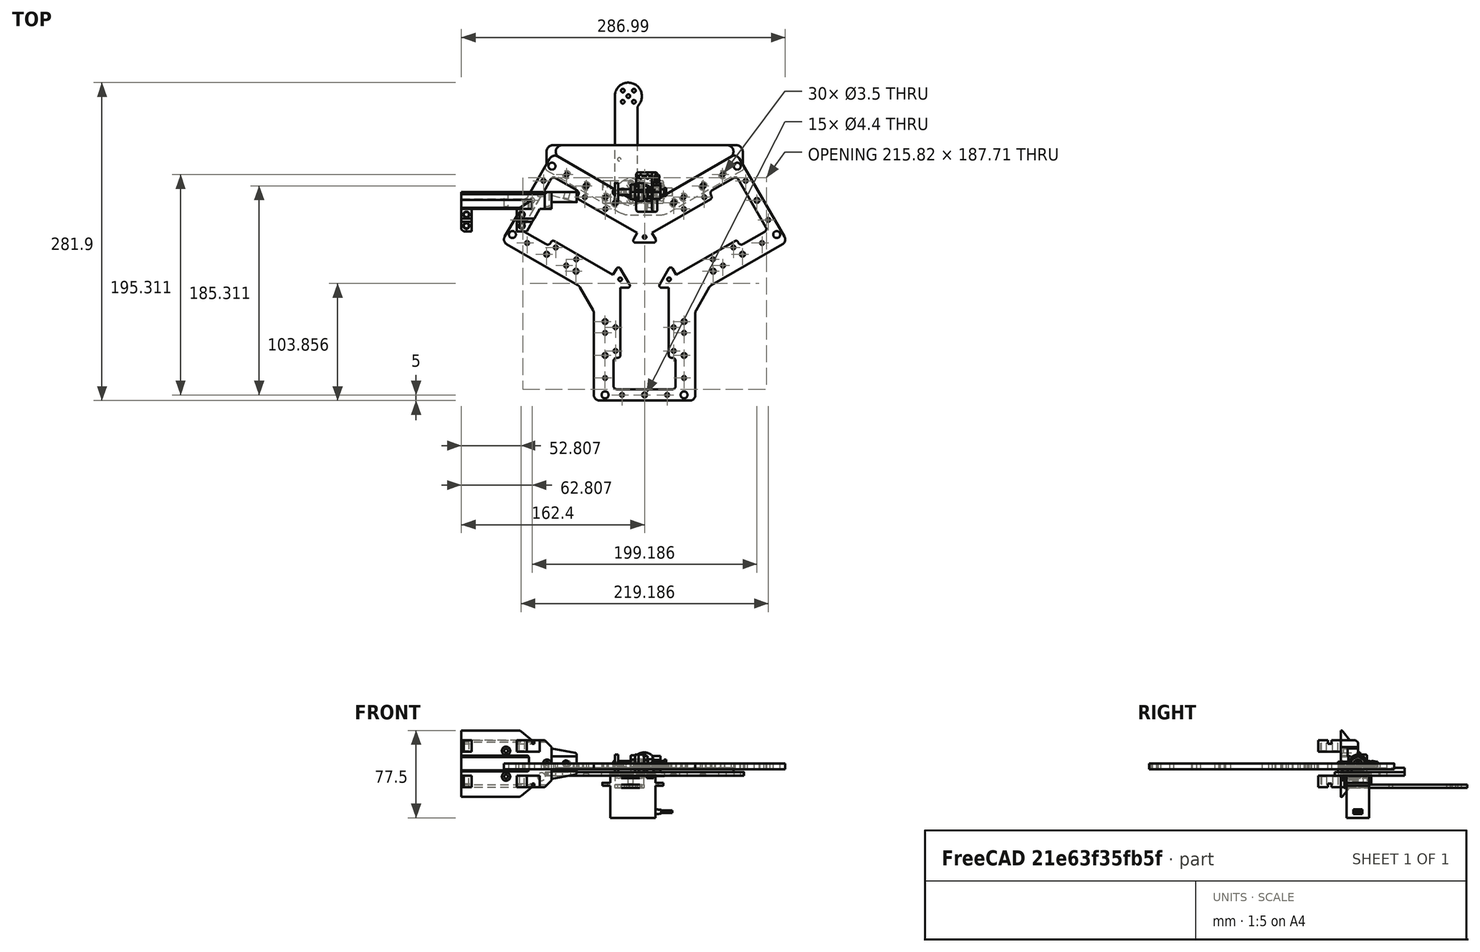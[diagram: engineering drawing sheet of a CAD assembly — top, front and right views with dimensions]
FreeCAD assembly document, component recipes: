
FREECAD ASSEMBLY — COMPONENT RECIPES ("twin-actuator")

This assembly document has 21 components, labeled P0..P20 below (a component is one placed body or linked part). 19 of them carry a construction recipe — the FreeCAD feature program that regenerates the part from scratch, quoted from this document or its linked companion documents; the rest are supplied as boundary geometry only. No exploded tour is included for this assembly.
COMPONENT P0 — recipe-attached ("Axe001", modeled in this document).
Construction recipe (the document's own serialized feature program — sketch geometry with constraints, then the solid features built on it; lengths are millimeters unless a unit is written):

FEATURE [Sketcher::SketchObject] Sketch
  ArcFitTolerance = 0
  AttachmentSupport = -> [XZ_Plane]
  ExternalTypes = [0]
  FullyConstrained = true
  MakeInternals = false
  MapMode = 5
  Placement = pos=(0,0,0) rot=(1,0,0;1.5708rad)
  sketch-geometry (14):
    g0: LineSegment StartX=0 StartY=2.5 StartZ=0 EndX=3 EndY=2.5 EndZ=0
    g1: LineSegment StartX=3 StartY=2.5 StartZ=0 EndX=3 EndY=3.5 EndZ=0
    g2: LineSegment StartX=3 StartY=3.5 StartZ=0 EndX=5 EndY=3.5 EndZ=0
    g3: LineSegment StartX=5 StartY=3.5 StartZ=0 EndX=5 EndY=1.5 EndZ=0
    g4: LineSegment StartX=5 StartY=1.5 StartZ=0 EndX=-9 EndY=1.5 EndZ=0
    g5: LineSegment StartX=-9 StartY=1.5 StartZ=0 EndX=-9 EndY=0 EndZ=0
    g6: LineSegment StartX=-9 StartY=0 StartZ=0 EndX=-37.5 EndY=0 EndZ=0
    g7: LineSegment StartX=-37.5 StartY=0 StartZ=0 EndX=-37.5 EndY=2.5 EndZ=0
    g8: LineSegment StartX=-37.5 StartY=2.5 StartZ=0 EndX=-11 EndY=2.5 EndZ=0
    g9: LineSegment StartX=-11 StartY=2.5 StartZ=0 EndX=-11 EndY=4 EndZ=0
    g10: LineSegment StartX=-11 StartY=4 StartZ=0 EndX=-7 EndY=4 EndZ=0
    g11: LineSegment StartX=-7 StartY=4 StartZ=0 EndX=-7 EndY=7.5 EndZ=0
    g12: LineSegment StartX=-7 StartY=7.5 StartZ=0 EndX=0 EndY=7.5 EndZ=0
    g13: LineSegment StartX=0 StartY=7.5 StartZ=0 EndX=0 EndY=2.5 EndZ=0
  constraints (42):
    c: PointOnObject(g0,g-2)
    c: Horizontal(g0)
    c: Coincident(g0,g1)
    c: Coincident(g1,g2)
    c: Horizontal(g2)
    c: Coincident(g2,g3)
    c: Vertical(g3)
    c: Coincident(g3,g4)
    c: Horizontal(g4)
    c: Coincident(g4,g5)
    c: Vertical(g5)
    c: Coincident(g5,g6)
    c: PointOnObject(g6,g-1)
    c: Horizontal(g6)
    c: Coincident(g6,g7)
    c: Vertical(g7)
    c: Coincident(g7,g8)
    c: Horizontal(g8)
    c: Coincident(g8,g9)
    c: Coincident(g9,g10)
    c: Horizontal(g10)
    c: Coincident(g10,g11)
    c: Vertical(g11)
    c: Coincident(g11,g12)
    c: Horizontal(g12)
    c: Coincident(g12,g13)
    c: Coincident(g13,g0)
    c: Vertical(g13)
    c: Vertical(g9)
    c: Vertical(g1)
    c: DistanceY(g2) = 3.5
    c: DistanceX(g2,g2) = 2
    c: DistanceX(g-1,g0) = 3
    c: DistanceY(g0) = 2.5
    c: DistanceX(g4,g4) = 14
    c: DistanceY(g3) = 1.5
    c: DistanceY(g10) = 4
    c: DistanceY(g12) = 7.5
    c: DistanceX(g12,g12) = 7
    c: DistanceX(g10,g10) = 4
    c: DistanceY(g8) = 2.5
    c: DistanceX(g6,g3) = 42.5
FEATURE [PartDesign::Revolution] Revolution
  Angle = 360
  Angle2 = 0
  Axis = (1,0,0)
  Base = (0,0,0)
  FuseOrder = 0
  Placement = pos=(0,0,0) rot=(1,0,0;1.5708rad)
  Profile = -> Sketch
  ReferenceAxis = -> X_Axis
  Refine = true
  Suppressed = false
  Type = 0
FEATURE [Sketcher::SketchObject] Sketch001
  ArcFitTolerance = 0
  AttachmentSupport = -> [YZ_Plane]
  ExternalGeometry = -> [Revolution]
  ExternalTypes = [0]
  FullyConstrained = true
  MakeInternals = false
  MapMode = 5
  Placement = pos=(0,0,0) rot=(0.57735,0.57735,0.57735;2.0944rad)
  sketch-geometry (7):
    g0: LineSegment StartX=6 StartY=3.4641 StartZ=0 EndX=0 EndY=6.9282 EndZ=0
    g1: LineSegment StartX=0 StartY=6.9282 StartZ=0 EndX=-6 EndY=3.4641 EndZ=0
    g2: LineSegment StartX=-6 StartY=3.4641 StartZ=0 EndX=-6 EndY=-3.4641 EndZ=0
    g3: LineSegment StartX=-6 StartY=-3.4641 StartZ=0 EndX=1.8723e-12 EndY=-6.9282 EndZ=0
    g4: LineSegment StartX=1.8723e-12 StartY=-6.9282 StartZ=0 EndX=6 EndY=-3.4641 EndZ=0
    g5: LineSegment StartX=6 StartY=-3.4641 StartZ=0 EndX=6 EndY=3.4641 EndZ=0
    g6: Circle [constr] CenterX=0 CenterY=0 CenterZ=0 NormalX=0 NormalY=0 NormalZ=1 AngleXU=0 Radius=6.9282
  constraints (16):
    c: Coincident(g0,g1)
    c: Coincident(g1,g2)
    c: Coincident(g2,g3)
    c: Coincident(g3,g4)
    c: Coincident(g4,g5)
    c: Coincident(g5,g0)
    c: Equal(g0, g1-g5) x5
    c: PointOnObject(g0,g6)
    c: PointOnObject(g1,g6)
    c: PointOnObject(g2,g6)
    c: PointOnObject(g3,g6)
    c: PointOnObject(g4,g6)
    c: PointOnObject(g5,g6)
    c: Coincident(g6,g-1)
    c: PointOnObject(g0,g-2)
    c: DistanceX(g1,g0) = 12
FEATURE [PartDesign::Pocket] Pocket
  BaseFeature = -> Revolution
  Direction = (-1,0,0)
  Length = 5
  Length2 = 100
  Placement = pos=(0,0,0) rot=(1,0,0;1.5708rad)
  Profile = -> Sketch001
  Refine = true
  SideType = 0
  Suppressed = false
  Type = 1
  Type2 = 0
FEATURE [Sketcher::SketchObject] Sketch002
  ArcFitTolerance = 0
  AttachmentSupport = -> [XZ_Plane]
  ExternalGeometry = -> [Pocket]
  ExternalTypes = [0]
  FullyConstrained = true
  MakeInternals = false
  MapMode = 5
  Placement = pos=(0,0,0) rot=(1,0,0;1.5708rad)
  sketch-geometry (2):
    g0: Circle CenterX=-3.5 CenterY=0 CenterZ=0 NormalX=0 NormalY=0 NormalZ=1 AngleXU=0 Radius=2.5
    g1: LineSegment [constr] StartX=-6e-16 StartY=-3.4641 StartZ=0 EndX=-7 EndY=3.4641 EndZ=0
  constraints (5):
    c: PointOnObject(g0,g-1)
    c: Diameter(g0) = 5
    c: Coincident(g1,g-4)
    c: Coincident(g1,g-3)
    c: PointOnObject(g0,g1)
FEATURE [PartDesign::Pocket] Pocket001
  BaseFeature = -> Pocket
  Direction = (0,1,-2e-16)
  Length = 5
  Length2 = 100
  Placement = pos=(0,0,0) rot=(1,0,0;1.5708rad)
  Profile = -> Sketch002
  Refine = true
  SideType = 2
  Suppressed = false
  Type = 1
  Type2 = 0
FEATURE [PartDesign::Chamfer] Chamfer
  Angle = 45
  Base = -> Pocket001 [Edge14,Edge21]
  BaseFeature = -> Pocket001
  ChamferType = 0
  FlipDirection = false
  Placement = pos=(0,0,0) rot=(1,0,0;1.5708rad)
  Refine = true
  Size = 0.2
  Size2 = 1
  SupportTransform = false
  Suppressed = false
  UseAllEdges = false
FEATURE [Sketcher::SketchObject] Sketch003
  ArcFitTolerance = 0
  AttachmentSupport = -> [Chamfer]
  ExternalTypes = [0]
  FullyConstrained = true
  MakeInternals = false
  MapMode = 5
  Placement = pos=(-37.5,0,0) rot=(0.707107,0,-0.707107;3.14159rad)
  sketch-geometry (1):
    g0: Circle CenterX=0 CenterY=0 CenterZ=0 NormalX=0 NormalY=0 NormalZ=1 AngleXU=0 Radius=1.5
  constraints (2):
    c: Coincident(g0,g-1)
    c: Diameter(g0) = 3
FEATURE [PartDesign::Pocket] Pocket002
  BaseFeature = -> Chamfer
  Direction = (1,0,2e-16)
  Length = 5
  Length2 = 100
  Placement = pos=(0,0,0) rot=(1,0,0;1.5708rad)
  Profile = -> Sketch003
  Refine = true
  SideType = 0
  Suppressed = false
  Type = 0
  Type2 = 0
FEATURE [PartDesign::Body] Body  label="Axe"
  AllowCompound = true
  Group = -> [Sketch,Revolution,Sketch001,Pocket,Sketch002,Pocket001,Chamfer,Sketch003,Pocket002]
  Origin = -> Origin105
  Placement = pos=(14.5,-1.72853e-06,0) rot=(0,0,1;0rad)
  Tip = -> Pocket002
COMPONENT P1 — same part as P0; its construction recipe is shown at P0.
COMPONENT P2 — recipe-attached ("Butée", modeled in this document).
Construction recipe (the document's own serialized feature program — sketch geometry with constraints, then the solid features built on it; lengths are millimeters unless a unit is written):

FEATURE [PartDesign::ShapeBinder] ShapeBinder001
  Placement = pos=(0.4,-64.9,0) rot=(0,0,1;3.14159rad)
  Support = -> [Part__Feature148]
  TraceSupport = false
FEATURE [Sketcher::SketchObject] Sketch265
  ArcFitTolerance = 1e-06
  AttachmentSupport = -> [ShapeBinder001]
  ExternalGeometry = -> [ShapeBinder001]
  ExternalTypes = [0,0,0,0,0,0,0,0,0]
  FullyConstrained = true
  MakeInternals = false
  MapMode = 5
  Placement = pos=(0.4,-64.9,-5) rot=(0,1,0;3.14159rad)
  sketch-geometry (12):
    g0: LineSegment [constr] StartX=0 StartY=34.0637 StartZ=0 EndX=-89.173 EndY=85.5477 EndZ=0
    g1: LineSegment [constr] StartX=0 StartY=34.0637 StartZ=0 EndX=0 EndY=106.471 EndZ=0
    g2: LineSegment StartX=0 StartY=106.471 StartZ=0 EndX=-87 EndY=106.471 EndZ=0
    g3: LineSegment StartX=-89.173 StartY=85.5477 StartZ=0 EndX=-87 EndY=89.3116 EndZ=0
    g4: LineSegment StartX=-87 StartY=89.3116 StartZ=0 EndX=-87 EndY=106.471 EndZ=0
    g5: LineSegment StartX=-89.173 StartY=85.5477 StartZ=0 EndX=-18.0263 EndY=44.4711 EndZ=0
    g6: LineSegment StartX=-18.0263 StartY=44.4711 StartZ=0 EndX=0 EndY=44.4711 EndZ=0
    g7: LineSegment StartX=0 StartY=44.4711 StartZ=0 EndX=0 EndY=106.471 EndZ=0
    g8: Circle CenterX=-69.1025 CenterY=80.3109 CenterZ=0 NormalX=0 NormalY=0 NormalZ=1 AngleXU=0 Radius=3.5
    g9: Circle CenterX=-34.4615 CenterY=60.3109 CenterZ=0 NormalX=0 NormalY=0 NormalZ=1 AngleXU=0 Radius=3.5
    g10: Circle CenterX=-51.782 CenterY=70.3109 CenterZ=0 NormalX=0 NormalY=0 NormalZ=1 AngleXU=0 Radius=1.7
    g11: Circle CenterX=-25.8013 CenterY=55.3109 CenterZ=0 NormalX=0 NormalY=0 NormalZ=1 AngleXU=0 Radius=1.7
  constraints (31):
    c: PointOnObject(g0,g-2)
    c: Coincident(g1,g0)
    c: PointOnObject(g1,g-2)
    c: Parallel(g0,g-8)
    c: Distance(g0,g-9) = 2
    c: Distance(g1,g-10) = 47
    c: Coincident(g2,g1)
    c: Horizontal(g2)
    c: PointOnObject(g0,g-11)
    c: Coincident(g3,g0)
    c: PointOnObject(g3,g-11)
    c: Coincident(g4,g3)
    c: Coincident(g4,g2)
    c: Vertical(g4)
    c: DistanceX(g2,g2) = 87
    c: Coincident(g5,g0)
    c: PointOnObject(g5,g0)
    c: Coincident(g6,g5)
    c: PointOnObject(g6,g1)
    c: Coincident(g7,g6)
    c: Coincident(g7,g1)
    c: Horizontal(g6)
    c: Distance(g-10,g6) = 15
    c: Coincident(g8,g-3)
    c: Coincident(g9,g-5)
    c: Equal(g8,g9)
    c: Diameter(g8) = 7
    c: Coincident(g10,g-4)
    c: Coincident(g11,g-6)
    c: Equal(g11,g10)
    c: Diameter(g10) = 3.4
FEATURE [PartDesign::Pad] Pad113
  Direction = (0,0,-1)
  Length = 3
  Length2 = 10
  Placement = pos=(0.4,-64.9,0) rot=(0,0,1;3.14159rad)
  Profile = -> Sketch265
  ReferenceAxis = -> Sketch265 [N_Axis]
  Refine = true
  SideType = 0
  Suppressed = false
  Type = 0
  Type2 = 0
FEATURE [PartDesign::Fillet] Fillet031
  Base = -> Pad113 [Edge11]
  BaseFeature = -> Pad113
  Placement = pos=(0.4,-64.9,0) rot=(0,0,1;3.14159rad)
  Radius = 6
  Refine = true
  SupportTransform = false
  Suppressed = false
  UseAllEdges = false
FEATURE [PartDesign::Fillet] Fillet032
  Base = -> Fillet031 [Edge31,Edge29]
  BaseFeature = -> Fillet031
  Placement = pos=(0.4,-64.9,0) rot=(0,0,1;3.14159rad)
  Radius = 3
  Refine = true
  SupportTransform = false
  Suppressed = false
  UseAllEdges = false
FEATURE [PartDesign::Fillet] Fillet033
  Base = -> Fillet032 [Edge30]
  BaseFeature = -> Fillet032
  Placement = pos=(0.4,-64.9,0) rot=(0,0,1;3.14159rad)
  Radius = 20
  Refine = true
  SupportTransform = false
  Suppressed = false
  UseAllEdges = false
FEATURE [Sketcher::SketchObject] Sketch266
  ArcFitTolerance = 1e-06
  AttachmentSupport = -> [Fillet033]
  ExternalGeometry = -> [ShapeBinder001,Fillet033]
  ExternalTypes = [0,0,0,0,0]
  FullyConstrained = true
  MakeInternals = false
  MapMode = 5
  Placement = pos=(0.4,-64.9,-5) rot=(0,0,1;3.14159rad)
  sketch-geometry (5):
    g0: LineSegment StartX=1.3e-14 StartY=-106.471 StartZ=0 EndX=7.3e-15 EndY=-59.4711 EndZ=0
    g1: LineSegment StartX=7.3e-15 StartY=-59.4711 StartZ=0 EndX=-11.6673 EndY=-59.4711 EndZ=0
    g2: LineSegment StartX=-14.1673 StartY=-60.141 StartZ=0 EndX=-75.8689 EndY=-95.7644 EndZ=0
    g3: LineSegment StartX=1.3e-14 StartY=-106.471 StartZ=0 EndX=-73 EndY=-106.471 EndZ=0
    g4: ArcOfCircle CenterX=-73 CenterY=-100.733 CenterZ=0 NormalX=0 NormalY=0 NormalZ=1 AngleXU=0 Radius=5.73771 StartAngle=2.0944 EndAngle=4.71239
  constraints (11):
    c: Coincident(g-7,g0)
    c: PointOnObject(g0,g-6)
    c: Coincident(g0,g1)
    c: Coincident(g1,g-5)
    c: Horizontal(g1)
    c: Tangent(g-4,g2) = -1.5708
    c: Coincident(g3,g0)
    c: PointOnObject(g3,g-7)
    c: Tangent(g4,g2) = -1.5708
    c: Tangent(g4,g3) = 1.5708
    c: DistanceX(g-7,g3) = 8
FEATURE [PartDesign::Pad] Pad114
  BaseFeature = -> Fillet033
  Direction = (0,0,1)
  Length = 4
  Length2 = 10
  Placement = pos=(0.4,-64.9,0) rot=(0,0,1;3.14159rad)
  Profile = -> Sketch266
  ReferenceAxis = -> Sketch266 [N_Axis]
  Refine = true
  SideType = 0
  Suppressed = false
  Type = 0
  Type2 = 0
FEATURE [PartDesign::Mirrored] Mirrored001
  BaseFeature = -> Pad114
  MirrorPlane = -> Sketch265 [V_Axis]
  Originals = -> [Pad113,Fillet031,Fillet032,Fillet033,Pad114]
  Placement = pos=(0.4,-64.9,0) rot=(0,0,1;3.14159rad)
  Refine = true
  Suppressed = false
  TransformMode = 1
FEATURE [PartDesign::Chamfer] Chamfer040
  Angle = 45
  Base = -> Mirrored001 [Edge92,Edge94,Edge96,Edge98]
  BaseFeature = -> Mirrored001
  ChamferType = 0
  FlipDirection = false
  Placement = pos=(0.4,-64.9,0) rot=(0,0,1;3.14159rad)
  Refine = true
  Size = 2
  Size2 = 1
  SupportTransform = false
  Suppressed = false
  UseAllEdges = false
FEATURE [PartDesign::Body] Body046  label="Butée"
  AllowCompound = true
  Group = -> [ShapeBinder001,Sketch265,Pad113,Fillet031,Fillet032,Fillet033,Sketch266,Pad114,Mirrored001,Chamfer040]
  Origin = -> Origin159
  Placement = pos=(0,0,-2.63) rot=(0,0,1;0rad)
  Tip = -> Chamfer040
COMPONENT P3 — recipe-attached ("Color_Sensor_Support001", modeled in this document).
Construction recipe (the document's own serialized feature program — sketch geometry with constraints, then the solid features built on it; lengths are millimeters unless a unit is written):

FEATURE [PartDesign::SubShapeBinder] Binder001
  BindCopyOnChange = 0
  BindMode = 0
  ClaimChildren = false
  Context = -> Part [Body045.Binder001.]
  Fuse = false
  MakeFace = true
  OffsetFill = false
  OffsetIntersection = false
  OffsetJoinType = 0
  OffsetOpenResult = false
  PartialLoad = false
  Refine = true
  Relative = true
  Support = -> [Link[Body.Fillet001.Face1]]
  _Version = 2
FEATURE [Sketcher::SketchObject] Sketch259
  ArcFitTolerance = 1e-06
  AttachmentSupport = -> [Origin157]
  ExternalGeometry = -> [Binder001]
  ExternalTypes = [0,0,0,0]
  FullyConstrained = true
  MakeInternals = false
  MapMode = 5
  sketch-geometry (6):
    g0: LineSegment StartX=-7 StartY=17.5 StartZ=0 EndX=-7 EndY=-17.5 EndZ=0
    g1: LineSegment StartX=-7 StartY=-17.5 StartZ=0 EndX=11.5 EndY=-17.5 EndZ=0
    g2: LineSegment StartX=11.5 StartY=-17.5 StartZ=0 EndX=11.5 EndY=17.5 EndZ=0
    g3: LineSegment StartX=11.5 StartY=17.5 StartZ=0 EndX=-7 EndY=17.5 EndZ=0
    g4: Circle CenterX=-3 CenterY=13.5 CenterZ=0 NormalX=0 NormalY=0 NormalZ=1 AngleXU=0 Radius=1.7
    g5: Circle CenterX=3 CenterY=13.5 CenterZ=0 NormalX=0 NormalY=0 NormalZ=1 AngleXU=0 Radius=1.7
  constraints (16):
    c: Coincident(g0,g1)
    c: Coincident(g1,g2)
    c: Coincident(g2,g3)
    c: Coincident(g3,g0)
    c: Vertical(g0)
    c: Vertical(g2)
    c: Horizontal(g1)
    c: Horizontal(g3)
    c: PointOnObject(g-3,g0)
    c: PointOnObject(g-4,g3)
    c: Distance(g2,g-5) = 4.5
    c: DistanceY(g0,g0) = 35
    c: Coincident(g4,g-6)
    c: Diameter(g4) = 3.4
    c: Equal(g5,g4)
    c: Symmetric(g5,g4,g-2)
FEATURE [PartDesign::Pad] Pad110
  Direction = (0,0,1)
  Length = 3
  Length2 = 10
  Profile = -> Sketch259
  ReferenceAxis = -> Sketch259 [N_Axis]
  Refine = true
  Reversed = true
  SideType = 0
  Suppressed = false
  Type = 0
  Type2 = 0
FEATURE [Sketcher::SketchObject] Sketch260
  ArcFitTolerance = 1e-06
  AttachmentSupport = -> [Pad110]
  ExternalGeometry = -> [Pad110]
  ExternalTypes = [0]
  FullyConstrained = true
  MakeInternals = false
  MapMode = 5
  sketch-geometry (4):
    g0: LineSegment StartX=11.5 StartY=17.5 StartZ=0 EndX=7 EndY=17.5 EndZ=0
    g1: LineSegment StartX=7 StartY=17.5 StartZ=0 EndX=7 EndY=-17.5 EndZ=0
    g2: LineSegment StartX=7 StartY=-17.5 StartZ=0 EndX=11.5 EndY=-17.5 EndZ=0
    g3: LineSegment StartX=11.5 StartY=-17.5 StartZ=0 EndX=11.5 EndY=17.5 EndZ=0
  constraints (10):
    c: Coincident(g0,g1)
    c: Coincident(g1,g2)
    c: Coincident(g2,g3)
    c: Coincident(g3,g0)
    c: Horizontal(g0)
    c: Horizontal(g2)
    c: Vertical(g1)
    c: Coincident(g0,g-3)
    c: Coincident(g2,g-3)
    c: Distance(g0,g0) = 4.5
FEATURE [PartDesign::Pad] Pad111
  BaseFeature = -> Pad110
  Direction = (0,0,1)
  Length = 1.6
  Length2 = 10
  Profile = -> Sketch260
  ReferenceAxis = -> Sketch260 [N_Axis]
  Refine = true
  SideType = 0
  Suppressed = false
  Type = 0
  Type2 = 0
FEATURE [PartDesign::Fillet] Fillet029
  Base = -> Pad111 [Edge2,Edge1,Edge15,Edge16]
  BaseFeature = -> Pad111
  Radius = 2
  Refine = true
  SupportTransform = false
  Suppressed = false
  UseAllEdges = false
FEATURE [Sketcher::SketchObject] Sketch261
  ArcFitTolerance = 1e-06
  AttachmentSupport = -> [Fillet029]
  ExternalTypes = [0]
  FullyConstrained = true
  MakeInternals = false
  MapMode = 5
  sketch-geometry (8):
    g0: ArcOfCircle CenterX=-5.52 CenterY=13.51 CenterZ=0 NormalX=0 NormalY=0 NormalZ=1 AngleXU=0 Radius=1 StartAngle=1.5708 EndAngle=4.71239
    g1: ArcOfCircle CenterX=5.52 CenterY=13.51 CenterZ=0 NormalX=0 NormalY=0 NormalZ=1 AngleXU=0 Radius=1 StartAngle=4.71239 EndAngle=7.85398
    g2: LineSegment StartX=-5.52 StartY=14.51 StartZ=0 EndX=5.52 EndY=14.51 EndZ=0
    g3: LineSegment StartX=-5.52 StartY=12.51 StartZ=0 EndX=5.52 EndY=12.51 EndZ=0
    g4: ArcOfCircle CenterX=-5.14 CenterY=-6.53 CenterZ=0 NormalX=0 NormalY=0 NormalZ=1 AngleXU=0 Radius=1.3 StartAngle=1.5708 EndAngle=4.71239
    g5: ArcOfCircle CenterX=5.14 CenterY=-6.53 CenterZ=0 NormalX=0 NormalY=0 NormalZ=1 AngleXU=0 Radius=1.3 StartAngle=4.71239 EndAngle=7.85398
    g6: LineSegment StartX=-5.14 StartY=-5.23 StartZ=0 EndX=5.14 EndY=-5.23 EndZ=0
    g7: LineSegment StartX=-5.14 StartY=-7.83 StartZ=0 EndX=5.14 EndY=-7.83 EndZ=0
  constraints (18):
    c: Tangent(g0,g2) = 1.5708
    c: Tangent(g0,g3) = -1.5708
    c: Tangent(g1,g2) = 1.5708
    c: Tangent(g1,g3) = -1.5708
    c: Equal(g0,g1)
    c: Tangent(g4,g6) = 1.5708
    c: Tangent(g4,g7) = -1.5708
    c: Tangent(g5,g6) = 1.5708
    c: Tangent(g5,g7) = -1.5708
    c: Equal(g4,g5)
    c: DistanceY(g-1,g1) = 13.51
    c: DistanceX(g-1,g1) = 5.52
    c: Radius(g1) = 1
    c: Symmetric(g0,g1,g-2)
    c: Symmetric(g4,g5,g-2)
    c: Radius(g5) = 1.3
    c: DistanceX(g4,g5) = 10.28
    c: Distance(g5,g-1) = 6.53
FEATURE [PartDesign::Pocket] Pocket041
  BaseFeature = -> Fillet029
  Direction = (0,0,-1)
  Length = 1
  Length2 = 5
  Profile = -> Sketch261
  ReferenceAxis = -> Sketch261 [N_Axis]
  Refine = true
  SideType = 0
  Suppressed = false
  Type = 0
  Type2 = 0
FEATURE [Sketcher::SketchObject] Sketch262
  ArcFitTolerance = 1e-06
  AttachmentSupport = -> [Pocket041]
  ExternalGeometry = -> [Pocket041]
  ExternalTypes = [0]
  FullyConstrained = true
  MakeInternals = false
  MapMode = 5
  Placement = pos=(0,0,-3) rot=(1,0,0;3.14159rad)
  sketch-geometry (4):
    g0: LineSegment StartX=8.5 StartY=17.5 StartZ=0 EndX=2.5 EndY=17.5 EndZ=0
    g1: LineSegment StartX=2.5 StartY=17.5 StartZ=0 EndX=2.5 EndY=7.5 EndZ=0
    g2: LineSegment StartX=2.5 StartY=7.5 StartZ=0 EndX=8.5 EndY=7.5 EndZ=0
    g3: LineSegment StartX=8.5 StartY=7.5 StartZ=0 EndX=8.5 EndY=17.5 EndZ=0
  constraints (12):
    c: Coincident(g0,g1)
    c: Coincident(g1,g2)
    c: Coincident(g2,g3)
    c: Coincident(g3,g0)
    c: Horizontal(g0)
    c: Horizontal(g2)
    c: Vertical(g1)
    c: Vertical(g3)
    c: PointOnObject(g0,g-3)
    c: Distance(g0,g-3) = 3
    c: Distance(g0,g0) = 6
    c: DistanceY(g1,g1) = 10
FEATURE [PartDesign::Pad] Pad112
  BaseFeature = -> Pocket041
  Direction = (0,0,-1)
  Length = 10
  Length2 = 10
  Profile = -> Sketch262
  ReferenceAxis = -> Sketch262 [N_Axis]
  Refine = true
  SideType = 0
  Suppressed = false
  Type = 0
  Type2 = 0
FEATURE [PartDesign::Draft] Draft005
  Angle = 30
  Base = -> Pad112 [Face26]
  BaseFeature = -> Pad112
  NeutralPlane = -> Pad112 [Face33]
  Refine = true
  Reversed = true
  SupportTransform = false
  Suppressed = false
FEATURE [PartDesign::Fillet] Fillet030
  Base = -> Draft005 [Edge36,Edge92,Edge96]
  BaseFeature = -> Draft005
  Radius = 6
  Refine = true
  SupportTransform = false
  Suppressed = false
  UseAllEdges = false
FEATURE [PartDesign::Chamfer] Chamfer037
  Angle = 45
  Base = -> Fillet030 [Edge2]
  BaseFeature = -> Fillet030
  ChamferType = 0
  FlipDirection = false
  Refine = true
  Size = 1
  Size2 = 1
  SupportTransform = false
  Suppressed = false
  UseAllEdges = false
FEATURE [Sketcher::SketchObject] Sketch263
  ArcFitTolerance = 1e-06
  AttachmentSupport = -> [Chamfer037]
  ExternalGeometry = -> [Chamfer037]
  ExternalTypes = [0,0]
  FullyConstrained = true
  MakeInternals = false
  MapMode = 5
  Placement = pos=(8.5,0,0) rot=(0.57735,0.57735,0.57735;2.0944rad)
  sketch-geometry (1):
    g0: Circle CenterX=-11.2321 CenterY=-7 CenterZ=0 NormalX=0 NormalY=0 NormalZ=1 AngleXU=0 Radius=2.3
  constraints (2):
    c: Symmetric(g-3,g-4,g0)
    c: Diameter(g0) = 4.6
FEATURE [PartDesign::Pocket] Pocket042
  BaseFeature = -> Chamfer037
  Direction = (-1,0,0)
  Length = 10
  Length2 = 5
  Profile = -> Sketch263
  ReferenceAxis = -> Sketch263 [N_Axis]
  Refine = true
  SideType = 0
  Suppressed = false
  Type = 0
  Type2 = 0
FEATURE [PartDesign::Chamfer] Chamfer038
  Angle = 45
  Base = -> Pocket042 [Edge42,Edge67]
  BaseFeature = -> Pocket042
  ChamferType = 0
  FlipDirection = false
  Refine = true
  Size = 0.4
  Size2 = 1
  SupportTransform = false
  Suppressed = false
  UseAllEdges = false
FEATURE [PartDesign::Chamfer] Chamfer039
  Angle = 45
  Base = -> Chamfer038 [Edge50,Edge36]
  BaseFeature = -> Chamfer038
  ChamferType = 0
  FlipDirection = false
  Refine = true
  Size = 1
  Size2 = 1
  SupportTransform = false
  Suppressed = false
  UseAllEdges = false
FEATURE [PartDesign::Body] Body045  label="ColorSensorSupport"
  AllowCompound = true
  Group = -> [Sketch259,Binder001,Pad110,Sketch260,Pad111,Fillet029,Sketch261,Pocket041,Sketch262,Pad112,Draft005,Fillet030,Chamfer037,Sketch263,Pocket042,Chamfer038,Chamfer039]
  Origin = -> Origin157
  Tip = -> Chamfer039
COMPONENT P4 — recipe-attached ("ConnecteurPneu001", modeled in this document).
Construction recipe (the document's own serialized feature program — sketch geometry with constraints, then the solid features built on it; lengths are millimeters unless a unit is written):

FEATURE [Sketcher::SketchObject] Sketch006
  ArcFitTolerance = 0
  AttachmentSupport = -> [XY_Plane002]
  ExternalTypes = [0]
  FullyConstrained = true
  MakeInternals = false
  MapMode = 5
  sketch-geometry (10):
    g0: LineSegment StartX=0 StartY=-4.5 StartZ=0 EndX=-2.5 EndY=-4.5 EndZ=0
    g1: LineSegment StartX=-2.5 StartY=-4.5 StartZ=0 EndX=-2.5 EndY=-1 EndZ=0
    g2: LineSegment StartX=-2.5 StartY=-1 StartZ=0 EndX=-2 EndY=-1 EndZ=0
    g3: LineSegment StartX=-2 StartY=-1 StartZ=0 EndX=-2 EndY=0 EndZ=0
    g4: LineSegment StartX=-2 StartY=0 StartZ=0 EndX=-4 EndY=0 EndZ=0
    g5: LineSegment StartX=-4 StartY=0 StartZ=0 EndX=-4 EndY=2.5 EndZ=0
    g6: LineSegment StartX=-4 StartY=2.5 StartZ=0 EndX=-2 EndY=2.5 EndZ=0
    g7: LineSegment StartX=-2 StartY=2.5 StartZ=0 EndX=-2 EndY=3.5 EndZ=0
    g8: LineSegment StartX=-2 StartY=3.5 StartZ=0 EndX=0 EndY=3.5 EndZ=0
    g9: LineSegment StartX=0 StartY=3.5 StartZ=0 EndX=0 EndY=-4.5 EndZ=0
  constraints (30):
    c: Horizontal(g0)
    c: Coincident(g0,g1)
    c: Vertical(g1)
    c: Coincident(g1,g2)
    c: Horizontal(g2)
    c: Coincident(g2,g3)
    c: PointOnObject(g3,g-1)
    c: Vertical(g3)
    c: Coincident(g3,g4)
    c: PointOnObject(g4,g-1)
    c: Coincident(g4,g5)
    c: Vertical(g5)
    c: Coincident(g5,g6)
    c: Horizontal(g6)
    c: Coincident(g6,g7)
    c: Vertical(g7)
    c: Coincident(g7,g8)
    c: Horizontal(g8)
    c: Coincident(g8,g9)
    c: Coincident(g9,g0)
    c: Vertical(g9)
    c: DistanceY(g5) = 2.5
    c: DistanceX(g3,g-1) = 2
    c: DistanceX(g0,g-1) = 2.5
    c: DistanceX(g4,g-1) = 4
    c: DistanceY(g7,g7) = 1
    c: DistanceY(g3,g3) = 1
    c: DistanceY(g0,g6) = 7
    c: DistanceX(g7,g-1) = 2
    c: PointOnObject(g0,g-2)
FEATURE [PartDesign::Revolution] Revolution003
  Angle = 360
  Angle2 = 0
  Axis = (0,1,0)
  Base = (0,0,0)
  FuseOrder = 0
  Profile = -> Sketch006
  ReferenceAxis = -> Sketch006 [V_Axis]
  Refine = true
  Suppressed = false
  Type = 0
FEATURE [Sketcher::SketchObject] Sketch007
  ArcFitTolerance = 0
  AttachmentSupport = -> [XY_Plane002]
  ExternalTypes = [0]
  FullyConstrained = true
  MakeInternals = false
  MapMode = 5
FEATURE [Sketcher::SketchObject] Sketch008
  ArcFitTolerance = 0
  AttachmentSupport = -> [XY_Plane002]
  ExternalGeometry = -> [Revolution003]
  ExternalTypes = [0]
  FullyConstrained = true
  MakeInternals = false
  MapMode = 5
  sketch-geometry (5):
    g0: LineSegment StartX=0 StartY=3.5 StartZ=0 EndX=-2.5 EndY=3.5 EndZ=0
    g1: LineSegment StartX=-2.5 StartY=3.5 StartZ=0 EndX=-2.5 EndY=4.5 EndZ=0
    g2: LineSegment StartX=-2.5 StartY=4.5 StartZ=0 EndX=-2 EndY=6.5 EndZ=0
    g3: LineSegment StartX=-2 StartY=6.5 StartZ=0 EndX=0 EndY=6.5 EndZ=0
    g4: LineSegment StartX=0 StartY=6.5 StartZ=0 EndX=0 EndY=3.5 EndZ=0
  constraints (15):
    c: PointOnObject(g0,g-2)
    c: Horizontal(g0)
    c: Coincident(g0,g1)
    c: Coincident(g1,g2)
    c: Coincident(g2,g3)
    c: PointOnObject(g3,g-2)
    c: Horizontal(g3)
    c: Coincident(g3,g4)
    c: Coincident(g0,g4)
    c: PointOnObject(g0,g-3)
    c: DistanceX(g0,g-1) = 2.5
    c: Vertical(g1)
    c: DistanceY(g4,g4) = 3
    c: DistanceX(g2,g0) = 2
    c: DistanceY(g1,g1) = 1
FEATURE [PartDesign::Revolution] Revolution004
  Angle = 360
  Angle2 = 0
  Axis = (0,1,0)
  Base = (0,0,0)
  BaseFeature = -> Revolution003
  FuseOrder = 0
  Profile = -> Sketch008
  ReferenceAxis = -> Sketch008 [V_Axis]
  Refine = true
  Suppressed = false
  Type = 0
FEATURE [PartDesign::LinearPattern] LinearPattern001
  BaseFeature = -> Revolution004
  Direction = -> Y_Axis002
  Length = 3
  Length2 = 100
  Mode = 0
  Mode2 = 0
  Occurrences = 2
  Occurrences2 = 1
  Offset = 3
  Offset2 = 10
  Originals = -> [Revolution004]
  Refine = true
  Reversed2 = false
  SpacingPattern = [0]
  SpacingPattern2 = [0]
  Spacings = [-1]
  Suppressed = false
  TransformMode = 0
FEATURE [Sketcher::SketchObject] Sketch009
  ArcFitTolerance = 0
  AttachmentSupport = -> [XZ_Plane002]
  ExternalTypes = [0]
  FullyConstrained = true
  MakeInternals = false
  MapMode = 5
  Placement = pos=(0,0,0) rot=(1,0,0;1.5708rad)
  sketch-geometry (1):
    g0: Circle CenterX=0 CenterY=0 CenterZ=0 NormalX=0 NormalY=0 NormalZ=1 AngleXU=0 Radius=1.5
  constraints (2):
    c: Coincident(g0,g-1)
    c: Diameter(g0) = 3
FEATURE [PartDesign::Pocket] Pocket004
  BaseFeature = -> LinearPattern001
  Direction = (0,1,-2e-16)
  Length = 5
  Length2 = 100
  Profile = -> Sketch009
  Refine = true
  SideType = 2
  Suppressed = false
  Type = 1
  Type2 = 0
FEATURE [PartDesign::Chamfer] Chamfer002
  Angle = 45
  Base = -> Pocket004 [Edge1,Edge3]
  BaseFeature = -> Pocket004
  ChamferType = 0
  FlipDirection = false
  Refine = true
  Size = 0.3
  Size2 = 1
  SupportTransform = false
  Suppressed = false
  UseAllEdges = false
FEATURE [Sketcher::SketchObject] Sketch010
  ArcFitTolerance = 0
  AttachmentSupport = -> [XZ_Plane002]
  ExternalGeometry = -> [Chamfer002]
  ExternalTypes = [0]
  FullyConstrained = true
  MakeInternals = false
  MapMode = 5
  Placement = pos=(0,0,0) rot=(1,0,0;1.5708rad)
  sketch-geometry (7):
    g0: LineSegment StartX=0 StartY=3.4641 StartZ=0 EndX=-3 EndY=1.73205 EndZ=0
    g1: LineSegment StartX=-3 StartY=1.73205 StartZ=0 EndX=-3 EndY=-1.73205 EndZ=0
    g2: LineSegment StartX=-3 StartY=-1.73205 StartZ=0 EndX=-5.997e-12 EndY=-3.4641 EndZ=0
    g3: LineSegment StartX=-5.997e-12 StartY=-3.4641 StartZ=0 EndX=3 EndY=-1.73205 EndZ=0
    g4: LineSegment StartX=3 StartY=-1.73205 StartZ=0 EndX=3 EndY=1.73205 EndZ=0
    g5: LineSegment StartX=3 StartY=1.73205 StartZ=0 EndX=0 EndY=3.4641 EndZ=0
    g6: Circle [constr] CenterX=0 CenterY=0 CenterZ=0 NormalX=0 NormalY=0 NormalZ=1 AngleXU=0 Radius=3.4641
  constraints (16):
    c: Coincident(g0,g1)
    c: Coincident(g1,g2)
    c: Coincident(g2,g3)
    c: Coincident(g3,g4)
    c: Coincident(g4,g5)
    c: Coincident(g5,g0)
    c: Equal(g0, g1-g5) x5
    c: PointOnObject(g0,g6)
    c: PointOnObject(g1,g6)
    c: PointOnObject(g2,g6)
    c: PointOnObject(g3,g6)
    c: PointOnObject(g4,g6)
    c: PointOnObject(g5,g6)
    c: Coincident(g6,g-1)
    c: PointOnObject(g0,g-2)
    c: DistanceX(g0,g4) = 6
FEATURE [PartDesign::Pocket] Pocket005
  BaseFeature = -> Chamfer002
  Direction = (0,1,-2e-16)
  Length = 5
  Length2 = 100
  Profile = -> Sketch010
  Refine = true
  SideType = 0
  Suppressed = false
  Type = 1
  Type2 = 0
FEATURE [PartDesign::Body] Body002  label="ConnecteurPneu"
  AllowCompound = true
  Group = -> [Sketch006,Revolution003,Sketch007,Sketch008,Revolution004,LinearPattern001,Sketch009,Pocket004,Chamfer002,Sketch010,Pocket005]
  Origin = -> Origin002
  Placement = pos=(11,6,0) rot=(0,0,1;0rad)
  Tip = -> Pocket005
COMPONENT P5 — same part as P4; its construction recipe is shown at P4.
COMPONENT P6 — recipe-attached ("ContreRotation001", modeled in this document).
Construction recipe (the document's own serialized feature program — sketch geometry with constraints, then the solid features built on it; lengths are millimeters unless a unit is written):

FEATURE [Sketcher::SketchObject] Sketch013
  ArcFitTolerance = 0
  AttachmentSupport = -> [YZ_Plane005]
  ExternalTypes = [0]
  FullyConstrained = true
  MakeInternals = false
  MapMode = 5
  Placement = pos=(0,0,0) rot=(0.57735,0.57735,0.57735;2.0944rad)
  sketch-geometry (5):
    g0: Circle CenterX=0 CenterY=0 CenterZ=0 NormalX=0 NormalY=0 NormalZ=1 AngleXU=0 Radius=1.6
    g1: ArcOfCircle CenterX=0 CenterY=0 CenterZ=0 NormalX=0 NormalY=0 NormalZ=1 AngleXU=0 Radius=8 StartAngle=0 EndAngle=3.14159
    g2: LineSegment StartX=-8 StartY=1e-15 StartZ=0 EndX=-8 EndY=-8 EndZ=0
    g3: LineSegment StartX=-8 StartY=-8 StartZ=0 EndX=8 EndY=-8 EndZ=0
    g4: LineSegment StartX=8 StartY=-8 StartZ=0 EndX=8 EndY=0 EndZ=0
  constraints (14):
    c: Coincident(g0,g-1)
    c: Diameter(g0) = 3.2
    c: Coincident(g1,g0)
    c: PointOnObject(g1,g-1)
    c: PointOnObject(g1,g-1)
    c: Coincident(g2,g1)
    c: Vertical(g2)
    c: Horizontal(g3)
    c: Coincident(g3,g4)
    c: Coincident(g4,g1)
    c: Vertical(g4)
    c: Coincident(g2,g3)
    c: Diameter(g1) = 16
    c: DistanceY(g3) = -8
FEATURE [PartDesign::Pad] Pad002
  Direction = (1,0,0)
  Length = 3
  Length2 = 100
  Placement = pos=(0,0,0) rot=(0.57735,0.57735,0.57735;2.0944rad)
  Profile = -> Sketch013
  Refine = true
  SideType = 0
  Suppressed = false
  Type = 0
  Type2 = 0
FEATURE [PartDesign::Fillet] Fillet001
  Base = -> Pad002 [Edge8,Edge5]
  BaseFeature = -> Pad002
  Placement = pos=(0,0,0) rot=(0.57735,0.57735,0.57735;2.0944rad)
  Radius = 1
  Refine = true
  SupportTransform = false
  Suppressed = false
  UseAllEdges = false
FEATURE [PartDesign::Body] Body004  label="ContreRotation"
  AllowCompound = true
  Group = -> [Sketch013,Pad002,Fillet001]
  Origin = -> Origin006
  Placement = pos=(-26,-2.62261e-06,3.05176e-05) rot=(1,0,0;1.5708rad)
  Tip = -> Fillet001
COMPONENT P7 — same part as P6; its construction recipe is shown at P6.
COMPONENT P8 — recipe-attached ("Coulisse001", modeled in this document).
Construction recipe (the document's own serialized feature program — sketch geometry with constraints, then the solid features built on it; lengths are millimeters unless a unit is written):

FEATURE [Sketcher::SketchObject] Sketch004
  ArcFitTolerance = 0
  AttachmentSupport = -> [XY_Plane001]
  ExternalTypes = [0]
  FullyConstrained = true
  MakeInternals = false
  MapMode = 5
  sketch-geometry (10):
    g0: LineSegment StartX=-12 StartY=2.5 StartZ=0 EndX=-12 EndY=4 EndZ=0
    g1: LineSegment StartX=-12 StartY=4 StartZ=0 EndX=-2 EndY=4 EndZ=0
    g2: LineSegment StartX=-2 StartY=4 StartZ=0 EndX=-2 EndY=3.25 EndZ=0
    g3: LineSegment StartX=-2 StartY=3.25 StartZ=0 EndX=0 EndY=3.25 EndZ=0
    g4: LineSegment StartX=0 StartY=3.25 StartZ=0 EndX=0 EndY=7.5 EndZ=0
    g5: LineSegment StartX=0 StartY=7.5 StartZ=0 EndX=3 EndY=7.5 EndZ=0
    g6: LineSegment StartX=3 StartY=7.5 StartZ=0 EndX=3 EndY=4 EndZ=0
    g7: LineSegment StartX=-12 StartY=2.5 StartZ=0 EndX=3.5 EndY=2.5 EndZ=0
    g8: LineSegment StartX=3.5 StartY=2.5 StartZ=0 EndX=3.5 EndY=4 EndZ=0
    g9: LineSegment StartX=3.5 StartY=4 StartZ=0 EndX=3 EndY=4 EndZ=0
  constraints (30):
    c: Vertical(g0)
    c: Coincident(g0,g1)
    c: Horizontal(g1)
    c: Coincident(g1,g2)
    c: Coincident(g2,g3)
    c: Horizontal(g3)
    c: Coincident(g3,g4)
    c: Vertical(g4)
    c: Coincident(g4,g5)
    c: Horizontal(g5)
    c: Coincident(g5,g6)
    c: Vertical(g6)
    c: Vertical(g2)
    c: DistanceY(g5) = 7.5
    c: DistanceX(g5,g5) = 3
    c: DistanceX(g1,g1) = 10
    c: DistanceY(g3) = 3.25
    c: DistanceY(g1) = 4
    c: Coincident(g0,g7)
    c: Horizontal(g7)
    c: Coincident(g7,g8)
    c: Vertical(g8)
    c: Coincident(g8,g9)
    c: Coincident(g9,g6)
    c: Horizontal(g9)
    c: DistanceY(g7) = 2.5
    c: PointOnObject(g3,g-2)
    c: DistanceX(g0,g7) = 15.5
    c: DistanceX(g6,g8) = 0.5
    c: DistanceY(g8) = 4
FEATURE [PartDesign::Revolution] Revolution002
  Angle = 360
  Angle2 = 0
  Axis = (1,0,0)
  Base = (0,0,0)
  FuseOrder = 0
  Profile = -> Sketch004
  ReferenceAxis = -> X_Axis001
  Refine = true
  Suppressed = false
  Type = 0
FEATURE [Sketcher::SketchObject] Sketch005
  ArcFitTolerance = 0
  AttachmentSupport = -> [YZ_Plane001]
  ExternalGeometry = -> [Revolution002]
  ExternalTypes = [0]
  FullyConstrained = true
  MakeInternals = false
  MapMode = 5
  Placement = pos=(0,0,0) rot=(0.57735,0.57735,0.57735;2.0944rad)
  sketch-geometry (7):
    g0: LineSegment StartX=0 StartY=6.9282 StartZ=0 EndX=-6 EndY=3.4641 EndZ=0
    g1: LineSegment StartX=-6 StartY=3.4641 StartZ=0 EndX=-6 EndY=-3.4641 EndZ=0
    g2: LineSegment StartX=-6 StartY=-3.4641 StartZ=0 EndX=0 EndY=-6.9282 EndZ=0
    g3: LineSegment StartX=0 StartY=-6.9282 StartZ=0 EndX=6 EndY=-3.4641 EndZ=0
    g4: LineSegment StartX=6 StartY=-3.4641 StartZ=0 EndX=6 EndY=3.4641 EndZ=0
    g5: LineSegment StartX=6 StartY=3.4641 StartZ=0 EndX=0 EndY=6.9282 EndZ=0
    g6: Circle [constr] CenterX=0 CenterY=0 CenterZ=0 NormalX=0 NormalY=0 NormalZ=1 AngleXU=0 Radius=6.9282
  constraints (16):
    c: Coincident(g0,g1)
    c: Coincident(g1,g2)
    c: Coincident(g2,g3)
    c: Coincident(g3,g4)
    c: Coincident(g4,g5)
    c: Coincident(g5,g0)
    c: Equal(g0, g1-g5) x5
    c: PointOnObject(g0,g6)
    c: PointOnObject(g1,g6)
    c: PointOnObject(g2,g6)
    c: PointOnObject(g3,g6)
    c: PointOnObject(g4,g6)
    c: PointOnObject(g5,g6)
    c: Coincident(g6,g-1)
    c: PointOnObject(g5,g-2)
    c: DistanceX(g0,g4) = 12
FEATURE [PartDesign::Pocket] Pocket003
  BaseFeature = -> Revolution002
  Direction = (-1,0,0)
  Length = 5
  Length2 = 100
  Profile = -> Sketch005
  Refine = true
  Reversed = true
  SideType = 0
  Suppressed = false
  Type = 1
  Type2 = 0
FEATURE [PartDesign::Chamfer] Chamfer001
  Angle = 45
  Base = -> Pocket003 [Edge2,Edge5]
  BaseFeature = -> Pocket003
  ChamferType = 0
  FlipDirection = false
  Refine = true
  Size = 0.3
  Size2 = 1
  SupportTransform = false
  Suppressed = false
  UseAllEdges = false
FEATURE [PartDesign::Body] Body001  label="Coulisse"
  AllowCompound = true
  Group = -> [Sketch004,Revolution002,Sketch005,Pocket003,Chamfer001]
  Origin = -> Origin001
  Placement = pos=(-3.8147e-06,9.095e-13,0) rot=(0,0,1;0rad)
  Tip = -> Chamfer001
COMPONENT P9 — same part as P8; its construction recipe is shown at P8.
COMPONENT P10 — geometry summary ("M3x10-Vis001"; no construction recipe available for this part):
  bounding box: 11.0 x 9.1 x 5.7 mm
  tessellated surface: 4,688 triangles
  volume: 89 mm^3 (16% of its bounding box)
  symmetry: mirror-symmetric across its z mid-plane
COMPONENT P11 — geometry summary ("M3x10-Vis002"; no construction recipe available for this part):
  bounding box: 11.7 x 5.7 x 5.7 mm
  tessellated surface: 4,688 triangles
  volume: 89 mm^3 (23% of its bounding box)
  symmetry: revolution-symmetric about the y axis through its bounding-box center; mirror-symmetric across its x mid-plane, z mid-plane
COMPONENT P12 — recipe-attached ("MG997", modeled in this document).
Construction recipe (the document's own serialized feature program — sketch geometry with constraints, then the solid features built on it; lengths are millimeters unless a unit is written):

FEATURE [Sketcher::SketchObject] Sketch086
  ArcFitTolerance = 0
  ExternalTypes = [0]
  FullyConstrained = true
  MakeInternals = false
  MapMode = 5
  Placement = pos=(0,0,0) rot=(1,0,0;1.5708rad)
  sketch-geometry (12):
    g0: LineSegment StartX=-37 StartY=-18.5 StartZ=0 EndX=-37 EndY=-16 EndZ=0
    g1: LineSegment StartX=-37 StartY=-16 StartZ=0 EndX=-30 EndY=-16 EndZ=0
    g2: LineSegment StartX=-30 StartY=-16 StartZ=0 EndX=-30 EndY=-8 EndZ=0
    g3: LineSegment StartX=-30 StartY=-8 StartZ=0 EndX=10 EndY=-8 EndZ=0
    g4: LineSegment StartX=10 StartY=-8 StartZ=0 EndX=10 EndY=-16 EndZ=0
    g5: LineSegment StartX=10 StartY=-16 StartZ=0 EndX=17 EndY=-16 EndZ=0
    g6: LineSegment StartX=17 StartY=-16 StartZ=0 EndX=17 EndY=-18.5 EndZ=0
    g7: LineSegment StartX=17 StartY=-18.5 StartZ=0 EndX=10 EndY=-18.5 EndZ=0
    g8: LineSegment StartX=10 StartY=-18.5 StartZ=0 EndX=10 EndY=-47 EndZ=0
    g9: LineSegment StartX=10 StartY=-47 StartZ=0 EndX=-30 EndY=-47 EndZ=0
    g10: LineSegment StartX=-30 StartY=-47 StartZ=0 EndX=-30 EndY=-18.5 EndZ=0
    g11: LineSegment StartX=-30 StartY=-18.5 StartZ=0 EndX=-37 EndY=-18.5 EndZ=0
  constraints (33):
    c: Vertical(g0)
    c: Coincident(g0,g1)
    c: Horizontal(g1)
    c: Coincident(g1,g2)
    c: Vertical(g2)
    c: Coincident(g2,g3)
    c: Horizontal(g3)
    c: Coincident(g3,g4)
    c: Coincident(g4,g5)
    c: Coincident(g5,g6)
    c: Vertical(g6)
    c: Coincident(g6,g7)
    c: Horizontal(g7)
    c: Coincident(g7,g8)
    c: Vertical(g8)
    c: Coincident(g8,g9)
    c: Horizontal(g9)
    c: Coincident(g9,g10)
    c: Coincident(g10,g11)
    c: Coincident(g11,g0)
    c: Horizontal(g11)
    c: Tangent(g4,g8) = -1.5708
    c: Tangent(g10,g2)
    c: Equal(g1,g5)
    c: Tangent(g1,g5)
    c: Equal(g6,g0)
    c: DistanceX(g-1,g3) = 10
    c: DistanceX(g0,g5) = 54
    c: DistanceX(g10,g7) = 40
    c: DistanceY(g9,g-1) = 47
    c: DistanceY(g3,g-1) = 8
    c: DistanceY(g6,g6) = 2.5
    c: DistanceY(g0,g-1) = 18.5
FEATURE [PartDesign::Pad] Pad050
  Direction = (0,-1,0)
  Length = 20
  Length2 = 100
  Placement = pos=(0,0,0) rot=(1,0,0;1.5708rad)
  Profile = -> Sketch086
  Refine = true
  SideType = 2
  Suppressed = false
  Type = 0
  Type2 = 0
FEATURE [Sketcher::SketchObject] Sketch087
  ArcFitTolerance = 0
  ExternalTypes = [0]
  FullyConstrained = true
  MakeInternals = false
  MapMode = 5
  sketch-geometry (4):
    g0: Circle CenterX=14.5 CenterY=5 CenterZ=0 NormalX=0 NormalY=0 NormalZ=1 AngleXU=0 Radius=2
    g1: Circle CenterX=14.5 CenterY=-5 CenterZ=0 NormalX=0 NormalY=0 NormalZ=1 AngleXU=0 Radius=2
    g2: Circle CenterX=-34.5 CenterY=5 CenterZ=0 NormalX=0 NormalY=0 NormalZ=1 AngleXU=0 Radius=2
    g3: Circle CenterX=-34.5 CenterY=-5 CenterZ=0 NormalX=0 NormalY=0 NormalZ=1 AngleXU=0 Radius=2
  constraints (10):
    c: Equal(g2,g3)
    c: Equal(g3,g1)
    c: Equal(g1,g0)
    c: Symmetric(g0,g1,g-1)
    c: Symmetric(g2,g3,g-1)
    c: Horizontal(g2,g0)
    c: Diameter(g0) = 4
    c: DistanceY(g1,g0) = 10
    c: DistanceX(g2,g0) = 49
    c: DistanceX(g-1,g0) = 14.5
FEATURE [PartDesign::Pocket] Pocket033
  BaseFeature = -> Pad050
  Direction = (0,0,-1)
  Length = 5
  Length2 = 100
  Placement = pos=(0,0,0) rot=(1,0,0;1.5708rad)
  Profile = -> Sketch087
  Refine = true
  SideType = 0
  Suppressed = false
  Type = 1
  Type2 = 0
FEATURE [PartDesign::Fillet] Fillet024
  Base = -> Pocket033 [Edge28,Edge19,Edge4,Edge3]
  BaseFeature = -> Pocket033
  Placement = pos=(0,0,0) rot=(1,0,0;1.5708rad)
  Radius = 1
  Refine = true
  SupportTransform = false
  Suppressed = false
  UseAllEdges = false
FEATURE [Sketcher::SketchObject] Sketch090
  ArcFitTolerance = 0
  AttachmentOffset = pos=(0,0,-2) rot=(0,0,1;0rad)
  ExternalTypes = [0]
  FullyConstrained = true
  MakeInternals = false
  MapMode = 5
  Placement = pos=(0,0,-2) rot=(0,0,1;0rad)
  sketch-geometry (1):
    g0: Circle CenterX=0 CenterY=0 CenterZ=0 NormalX=0 NormalY=0 NormalZ=1 AngleXU=0 Radius=3
  constraints (2):
    c: Coincident(g0,g-1)
    c: Diameter(g0) = 6
FEATURE [PartDesign::Pad] Pad053
  Direction = (0,0,1)
  Length = 10
  Length2 = 100
  Placement = pos=(0,0,-2) rot=(0,0,1;0rad)
  Profile = -> Sketch090
  Refine = true
  Reversed = true
  SideType = 0
  Suppressed = false
  Type = 0
  Type2 = 0
FEATURE [PartDesign::Chamfer] Chamfer029
  Angle = 45
  Base = -> Pad053 [Edge2]
  BaseFeature = -> Pad053
  ChamferType = 0
  FlipDirection = false
  Placement = pos=(0,0,-2) rot=(0,0,1;0rad)
  Refine = true
  Size = 0.5
  Size2 = 1
  SupportTransform = false
  Suppressed = false
  UseAllEdges = false
FEATURE [PartDesign::Body] Body043  label="ServoAxis001"
  AllowCompound = true
  Group = -> [Sketch090,Pad053,Chamfer029]
  Origin = -> Origin064
  Tip = -> Chamfer029
FEATURE [Sketcher::SketchObject] Sketch235
  ArcFitTolerance = 0
  AttachmentSupport = -> [Fillet024]
  ExternalTypes = [0]
  FullyConstrained = true
  MakeInternals = false
  MapMode = 5
  Placement = pos=(0,9e-16,-8) rot=(0,0,1;3.14159rad)
  sketch-geometry (1):
    g0: Circle CenterX=0 CenterY=0 CenterZ=0 NormalX=0 NormalY=0 NormalZ=1 AngleXU=0 Radius=6.5
  constraints (2):
    c: Coincident(g0,g-1)
    c: Diameter(g0) = 13
FEATURE [PartDesign::Pad] Pad096
  BaseFeature = -> Fillet024
  Direction = (0,0,1)
  Length = 2
  Length2 = 10
  Placement = pos=(0,0,0) rot=(1,0,0;1.5708rad)
  Profile = -> Sketch235
  ReferenceAxis = -> Sketch235 [N_Axis]
  Refine = true
  SideType = 0
  Suppressed = false
  Type = 0
  Type2 = 0
FEATURE [PartDesign::Fillet] Fillet011
  Base = -> Pad096 [Edge61]
  BaseFeature = -> Pad096
  Placement = pos=(0,0,0) rot=(1,0,0;1.5708rad)
  Radius = 1
  Refine = true
  SupportTransform = false
  Suppressed = false
  UseAllEdges = false
FEATURE [Sketcher::SketchObject] Sketch245
  ArcFitTolerance = 1e-06
  AttachmentSupport = -> [Fillet011]
  ExternalGeometry = -> [Fillet011]
  ExternalTypes = [0]
  FullyConstrained = true
  MakeInternals = false
  MapMode = 5
  Placement = pos=(10,0,0) rot=(0.707107,0,0.707107;3.14159rad)
  sketch-geometry (5):
    g0: LineSegment StartX=-43.7 StartY=4 StartZ=0 EndX=-43.7 EndY=-4 EndZ=0
    g1: LineSegment StartX=-43.7 StartY=-4 StartZ=0 EndX=-39.5 EndY=-4 EndZ=0
    g2: LineSegment StartX=-39.5 StartY=-4 StartZ=0 EndX=-39.5 EndY=4 EndZ=0
    g3: LineSegment StartX=-39.5 StartY=4 StartZ=0 EndX=-43.7 EndY=4 EndZ=0
    g4: GeomPoint [constr] X=-41.6 Y=0 Z=0
  constraints (13):
    c: Coincident(g0,g1)
    c: Coincident(g1,g2)
    c: Coincident(g2,g3)
    c: Coincident(g3,g0)
    c: Vertical(g0)
    c: Vertical(g2)
    c: Horizontal(g1)
    c: Horizontal(g3)
    c: Symmetric(g2,g0,g4)
    c: PointOnObject(g4,g-1)
    c: Distance(g3,g3) = 4.2
    c: DistanceY(g0,g0) = 8
    c: Distance(g-3,g0) = 3.3
FEATURE [PartDesign::Pad] Pad103
  BaseFeature = -> Fillet011
  Direction = (1,0,-2e-16)
  Length = 5
  Length2 = 10
  Placement = pos=(0,0,0) rot=(1,0,0;1.5708rad)
  Profile = -> Sketch245
  ReferenceAxis = -> Sketch245 [N_Axis]
  Refine = true
  SideType = 0
  Suppressed = false
  TaperAngle = -4
  Type = 0
  Type2 = 0
FEATURE [Sketcher::SketchObject] Sketch246
  ArcFitTolerance = 1e-06
  AttachmentSupport = -> [Pad103]
  ExternalGeometry = -> [Pad103]
  ExternalTypes = [0,0]
  FullyConstrained = true
  MakeInternals = false
  MapMode = 5
  Placement = pos=(15,0,0) rot=(0.707107,0,0.707107;3.14159rad)
  sketch-geometry (4):
    g0: Circle CenterX=-41.6 CenterY=2.30024 CenterZ=0 NormalX=0 NormalY=0 NormalZ=1 AngleXU=0 Radius=1.15012
    g1: Circle CenterX=-41.6 CenterY=-1.38e-14 CenterZ=0 NormalX=0 NormalY=0 NormalZ=1 AngleXU=0 Radius=1.15012
    g2: Circle CenterX=-41.6 CenterY=-2.30024 CenterZ=0 NormalX=0 NormalY=0 NormalZ=1 AngleXU=0 Radius=1.15012
    g3: LineSegment [constr] StartX=-41.6 StartY=2.30024 StartZ=0 EndX=-41.6 EndY=-2.30024 EndZ=0
  constraints (10):
    c: Equal(g2,g1)
    c: Equal(g1,g0)
    c: Tangent(g0,g1)
    c: Tangent(g1,g2)
    c: Coincident(g3,g0)
    c: Coincident(g3,g2)
    c: Vertical(g3)
    c: PointOnObject(g1,g3)
    c: Symmetric(g-4,g-3,g1)
    c: Distance(g0,g-3) = 0.2
FEATURE [PartDesign::Pad] Pad104
  BaseFeature = -> Pad103
  Direction = (1,0,-2e-16)
  Length = 10
  Length2 = 10
  Placement = pos=(0,0,0) rot=(1,0,0;1.5708rad)
  Profile = -> Sketch246
  ReferenceAxis = -> Sketch246 [N_Axis]
  Refine = true
  SideType = 0
  Suppressed = false
  Type = 0
  Type2 = 0
FEATURE [PartDesign::Body] Body041  label="ServoBody001"
  AllowCompound = true
  Group = -> [Sketch086,Pad050,Sketch087,Pocket033,Fillet024,Sketch235,Pad096,Fillet011,Sketch245,Pad103,Sketch246,Pad104]
  Origin = -> Origin062
  Placement = pos=(0,0,-1) rot=(0,0,1;0rad)
  Tip = -> Pad104
COMPONENT P13 — same part as P12; its construction recipe is shown at P12.
COMPONENT P14 — recipe-attached ("RoundServoHorn001", modeled in this document).
Construction recipe (the document's own serialized feature program — sketch geometry with constraints, then the solid features built on it; lengths are millimeters unless a unit is written):

FEATURE [Sketcher::SketchObject] Sketch088
  ArcFitTolerance = 0
  ExternalTypes = [0]
  FullyConstrained = true
  MakeInternals = false
  MapMode = 5
  sketch-geometry (7):
    g0: Circle CenterX=0 CenterY=0 CenterZ=0 NormalX=0 NormalY=0 NormalZ=1 AngleXU=0 Radius=10
    g1: Circle CenterX=0 CenterY=7 CenterZ=0 NormalX=0 NormalY=0 NormalZ=1 AngleXU=0 Radius=1.5
    g2: Circle CenterX=7 CenterY=0 CenterZ=0 NormalX=0 NormalY=0 NormalZ=1 AngleXU=0 Radius=1.5
    g3: Circle CenterX=0 CenterY=-7 CenterZ=0 NormalX=0 NormalY=0 NormalZ=1 AngleXU=0 Radius=1.5
    g4: Circle CenterX=-7 CenterY=0 CenterZ=0 NormalX=0 NormalY=0 NormalZ=1 AngleXU=0 Radius=1.5
    g5: Circle [constr] CenterX=0 CenterY=0 CenterZ=0 NormalX=0 NormalY=0 NormalZ=1 AngleXU=0 Radius=7
    g6: Circle CenterX=0 CenterY=0 CenterZ=0 NormalX=0 NormalY=0 NormalZ=1 AngleXU=0 Radius=1.5
  constraints (18):
    c: Coincident(g0,g-1)
    c: Diameter(g0) = 20
    c: PointOnObject(g1,g-2)
    c: PointOnObject(g2,g-1)
    c: PointOnObject(g3,g-2)
    c: PointOnObject(g4,g-1)
    c: Equal(g4,g1)
    c: Equal(g1,g2)
    c: Equal(g2,g3)
    c: Diameter(g1) = 3
    c: Coincident(g5,g0)
    c: PointOnObject(g1,g5)
    c: PointOnObject(g2,g5)
    c: PointOnObject(g3,g5)
    c: PointOnObject(g4,g5)
    c: DistanceX(g4,g2) = 14
    c: Coincident(g6,g0)
    c: Equal(g2,g6)
FEATURE [PartDesign::Pad] Pad052
  Direction = (0,0,1)
  Length = 2
  Length2 = 100
  Profile = -> Sketch088
  Refine = true
  Reversed = true
  SideType = 0
  Suppressed = false
  Type = 0
  Type2 = 0
FEATURE [Sketcher::SketchObject] Sketch089
  ArcFitTolerance = 0
  ExternalTypes = [0]
  FullyConstrained = true
  MakeInternals = false
  MapMode = 5
  sketch-geometry (2):
    g0: Circle CenterX=0 CenterY=0 CenterZ=0 NormalX=0 NormalY=0 NormalZ=1 AngleXU=0 Radius=4.7
    g1: Circle CenterX=0 CenterY=0 CenterZ=0 NormalX=0 NormalY=0 NormalZ=1 AngleXU=0 Radius=3
  constraints (4):
    c: Coincident(g0,g-1)
    c: Coincident(g1,g0)
    c: Diameter(g0) = 9.4
    c: Diameter(g1) = 6
FEATURE [PartDesign::Pad] Pad051
  BaseFeature = -> Pad052
  Direction = (0,0,1)
  Length = 5.4
  Length2 = 100
  Profile = -> Sketch089
  Refine = true
  Reversed = true
  SideType = 0
  Suppressed = false
  Type = 0
  Type2 = 0
FEATURE [PartDesign::Body] Body042  label="RoundServoHorn"
  AllowCompound = true
  Group = -> [Sketch088,Pad052,Sketch089,Pad051]
  Origin = -> Origin063
  Placement = pos=(0,0,0) rot=(1,0,0;1.5708rad)
  Tip = -> Pad051
COMPONENT P15 — same part as P14; its construction recipe is shown at P14.
COMPONENT P16 — recipe-attached ("SupportBras001", modeled in this document).
Construction recipe (the document's own serialized feature program — sketch geometry with constraints, then the solid features built on it; lengths are millimeters unless a unit is written):

FEATURE [Sketcher::SketchObject] Sketch014
  ArcFitTolerance = 0
  AttachmentSupport = -> [YZ_Plane087]
  ExternalTypes = [0]
  FullyConstrained = true
  MakeInternals = false
  MapMode = 5
  Placement = pos=(0,0,0) rot=(0.57735,0.57735,0.57735;2.0944rad)
  sketch-geometry (5):
    g0: ArcOfCircle CenterX=0 CenterY=0 CenterZ=0 NormalX=0 NormalY=0 NormalZ=1 AngleXU=0 Radius=8 StartAngle=2e-16 EndAngle=3.14159
    g1: LineSegment StartX=-8 StartY=4.01e-14 StartZ=0 EndX=-8 EndY=-8 EndZ=0
    g2: LineSegment StartX=-8 StartY=-8 StartZ=0 EndX=8 EndY=-8 EndZ=0
    g3: LineSegment StartX=8 StartY=-8 StartZ=0 EndX=8 EndY=1.8e-15 EndZ=0
    g4: Circle CenterX=0 CenterY=0 CenterZ=0 NormalX=0 NormalY=0 NormalZ=1 AngleXU=0 Radius=4.15
  constraints (14):
    c: Coincident(g0,g-1)
    c: PointOnObject(g0,g-1)
    c: PointOnObject(g0,g-1)
    c: Coincident(g1,g0)
    c: Coincident(g1,g2)
    c: Horizontal(g2)
    c: Coincident(g2,g3)
    c: Coincident(g3,g0)
    c: Vertical(g3)
    c: Vertical(g1)
    c: Diameter(g0) = 16
    c: DistanceY(g2) = -8
    c: Coincident(g4,g0)
    c: Diameter(g4) = 8.3
FEATURE [PartDesign::Pad] Pad003
  Direction = (1,0,0)
  Length = 8
  Length2 = 100
  Placement = pos=(0,0,0) rot=(0.57735,0.57735,0.57735;2.0944rad)
  Profile = -> Sketch014
  ReferenceAxis = -> Sketch014 [N_Axis]
  Refine = true
  Reversed = true
  SideType = 0
  Suppressed = false
  Type = 0
  Type2 = 0
FEATURE [Sketcher::SketchObject] Sketch015
  ArcFitTolerance = 0
  AttachmentSupport = -> [Pad003]
  ExternalGeometry = -> [Pad003]
  ExternalTypes = [0]
  FullyConstrained = true
  MakeInternals = false
  MapMode = 5
  Placement = pos=(0,-1.8e-15,-8) rot=(0.707107,0.707107,0;3.14159rad)
  sketch-geometry (19):
    g0: LineSegment StartX=-8 StartY=-26 StartZ=0 EndX=8 EndY=-26 EndZ=0
    g1: Circle [constr] CenterX=0 CenterY=-12 CenterZ=0 NormalX=0 NormalY=0 NormalZ=1 AngleXU=0 Radius=10
    g2: LineSegment [constr] StartX=-8 StartY=0 StartZ=0 EndX=8 EndY=0 EndZ=0
    g3: LineSegment StartX=-8 StartY=0 StartZ=0 EndX=-8 EndY=-3.05573 EndZ=0
    g4: LineSegment StartX=8 StartY=0 StartZ=0 EndX=8 EndY=-3.05573 EndZ=0
    g5: LineSegment StartX=8 StartY=-26 StartZ=0 EndX=8 EndY=-20.9443 EndZ=0
    g6: LineSegment StartX=-8 StartY=-26 StartZ=0 EndX=-8 EndY=-20.9443 EndZ=0
    g7: ArcOfCircle CenterX=0 CenterY=-12 CenterZ=0 NormalX=0 NormalY=0 NormalZ=1 AngleXU=0 Radius=12 StartAngle=2.30052 EndAngle=3.98266
    g8: ArcOfCircle CenterX=0 CenterY=-12 CenterZ=0 NormalX=0 NormalY=0 NormalZ=1 AngleXU=0 Radius=12 StartAngle=5.44212 EndAngle=7.12425
    g9: Circle CenterX=-7 CenterY=-12 CenterZ=0 NormalX=0 NormalY=0 NormalZ=1 AngleXU=0 Radius=2.25
    g10: Circle CenterX=7 CenterY=-12 CenterZ=0 NormalX=0 NormalY=0 NormalZ=1 AngleXU=0 Radius=2.25
    g11: Circle [constr] CenterX=0 CenterY=-19 CenterZ=0 NormalX=0 NormalY=0 NormalZ=1 AngleXU=0 Radius=2.25
    g12: Circle [constr] CenterX=0 CenterY=-5 CenterZ=0 NormalX=0 NormalY=0 NormalZ=1 AngleXU=0 Radius=2.25
    g13: Circle [constr] CenterX=0 CenterY=-12 CenterZ=0 NormalX=0 NormalY=0 NormalZ=1 AngleXU=0 Radius=7
    g14: LineSegment [constr] StartX=-7 StartY=-12 StartZ=0 EndX=7 EndY=-12 EndZ=0
    g15: Circle [constr] CenterX=0 CenterY=-12 CenterZ=0 NormalX=0 NormalY=0 NormalZ=1 AngleXU=0 Radius=2.25
    g16: LineSegment StartX=-8 StartY=0 StartZ=0 EndX=-8 EndY=18 EndZ=0
    g17: LineSegment StartX=-8 StartY=18 StartZ=0 EndX=8 EndY=18 EndZ=0
    g18: LineSegment StartX=8 StartY=18 StartZ=0 EndX=8 EndY=0 EndZ=0
  constraints (51):
    c: Symmetric(g0,g0,g-2)
    c: DistanceY(g0,g-1) = 26
    c: PointOnObject(g1,g-2)
    c: DistanceY(g1,g-1) = 12
    c: Diameter(g1) = 20
    c: PointOnObject(g2,g-1)
    c: Equal(g0,g2)
    c: Symmetric(g2,g2,g-2)
    c: Coincident(g2,g3)
    c: Vertical(g3)
    c: Coincident(g2,g4)
    c: Vertical(g4)
    c: Coincident(g0,g5)
    c: Vertical(g5)
    c: Coincident(g0,g6)
    c: Vertical(g6)
    c: Coincident(g7,g1)
    c: Coincident(g7,g3)
    c: Coincident(g7,g6)
    c: Coincident(g8,g7)
    c: Coincident(g8,g4)
    c: Coincident(g8,g5)
    c: DistanceX(g2,g2) = 16
    c: Diameter(g8) = 24
    c: PointOnObject(g11,g-2)
    c: PointOnObject(g12,g-2)
    c: Coincident(g13,g7)
    c: PointOnObject(g12,g13)
    c: PointOnObject(g10,g13)
    c: PointOnObject(g11,g13)
    c: PointOnObject(g9,g13)
    c: Diameter(g13) = 14
    c: Diameter(g12) = 4.5
    c: Equal(g12,g11)
    c: Equal(g12,g10)
    c: Equal(g12,g9)
    c: Coincident(g14,g9)
    c: Coincident(g14,g10)
    c: Horizontal(g14)
    c: PointOnObject(g7,g14)
    c: Equal(g3,g4)
    c: Coincident(g15,g7)
    c: Equal(g15,g10)
    c: Coincident(g16,g2)
    c: Vertical(g16)
    c: Coincident(g17,g16)
    c: Horizontal(g17)
    c: Coincident(g18,g17)
    c: Coincident(g18,g2)
    c: Vertical(g18)
    c: DistanceY(g18,g18) = 18
FEATURE [PartDesign::Pad] Pad004
  BaseFeature = -> Pad003
  Direction = (0,0,-1)
  Length = 10.5
  Length2 = 100
  Placement = pos=(0,0,0) rot=(0.57735,0.57735,0.57735;2.0944rad)
  Profile = -> Sketch015
  ReferenceAxis = -> Sketch015 [N_Axis]
  Refine = true
  SideType = 0
  Suppressed = false
  Type = 0
  Type2 = 0
FEATURE [PartDesign::Chamfer] Chamfer004
  Angle = 45
  Base = -> Pad004 [Edge20,Edge21,Edge38,Edge39]
  BaseFeature = -> Pad004
  ChamferType = 0
  FlipDirection = false
  Placement = pos=(0,0,0) rot=(0.57735,0.57735,0.57735;2.0944rad)
  Refine = true
  Size = 0.4
  Size2 = 1
  SupportTransform = false
  Suppressed = false
  UseAllEdges = false
FEATURE [PartDesign::Fillet] Fillet002
  Base = -> Chamfer004 [Edge35,Edge13,Edge28,Edge22,Edge20,Edge18,Edge16,Edge14]
  BaseFeature = -> Chamfer004
  Placement = pos=(0,0,0) rot=(0.57735,0.57735,0.57735;2.0944rad)
  Radius = 3
  Refine = true
  SupportTransform = false
  Suppressed = false
  UseAllEdges = false
FEATURE [Sketcher::SketchObject] Sketch258
  ArcFitTolerance = 1e-06
  AttachmentSupport = -> [Fillet002]
  ExternalGeometry = -> [Fillet002]
  ExternalTypes = [0,0,0]
  FullyConstrained = true
  MakeInternals = false
  MapMode = 5
  Placement = pos=(0,0,-18.5) rot=(0.707107,0.707107,0;3.14159rad)
  sketch-geometry (5):
    g0: ArcOfCircle CenterX=-5e-15 CenterY=-12 CenterZ=0 NormalX=0 NormalY=0 NormalZ=1 AngleXU=0 Radius=12 StartAngle=0.747584 EndAngle=2.39401
    g1: LineSegment [constr] StartX=-8.8 StartY=-3.84157 StartZ=0 EndX=8.8 EndY=-3.84157 EndZ=0
    g2: LineSegment StartX=8.8 StartY=-3.84157 StartZ=0 EndX=8.8 EndY=18 EndZ=0
    g3: LineSegment StartX=8.8 StartY=18 StartZ=0 EndX=-8.8 EndY=18 EndZ=0
    g4: LineSegment StartX=-8.8 StartY=18 StartZ=0 EndX=-8.8 EndY=-3.84157 EndZ=0
  constraints (13):
    c: Coincident(g0,g-3)
    c: Coincident(g0,g-4)
    c: PointOnObject(g-1,g0)
    c: Coincident(g1,g2)
    c: Coincident(g2,g3)
    c: Coincident(g3,g4)
    c: Coincident(g4,g1)
    c: Horizontal(g3)
    c: Vertical(g2)
    c: Vertical(g4)
    c: Coincident(g1,g0)
    c: Coincident(g1,g0)
    c: PointOnObject(g-5,g3)
FEATURE [PartDesign::Pocket] Pocket040
  BaseFeature = -> Fillet002
  Direction = (0,0,1)
  Length = 7.5
  Length2 = 5
  Placement = pos=(0,0,0) rot=(0.57735,0.57735,0.57735;2.0944rad)
  Profile = -> Sketch258
  ReferenceAxis = -> Sketch258 [N_Axis]
  Refine = true
  SideType = 0
  Suppressed = false
  Type = 0
  Type2 = 0
FEATURE [PartDesign::Body] Body005  label="SupportBras"
  AllowCompound = true
  Group = -> [Sketch014,Pad003,Sketch015,Pad004,Chamfer004,Fillet002,Sketch258,Pocket040]
  Origin = -> Origin139
  Tip = -> Pocket040
COMPONENT P17 — same part as P16; its construction recipe is shown at P16.
COMPONENT P18 — recipe-attached ("arm-plate001", modeled in this document).
Construction recipe (the document's own serialized feature program — sketch geometry with constraints, then the solid features built on it; lengths are millimeters unless a unit is written):

FEATURE [PartDesign::ShapeBinder] ShapeBinder
  Placement = pos=(3.5e-15,-1.2e-15,-10.5) rot=(0,0,1;0rad)
  Support = -> [Fillet002]
  TraceSupport = false
FEATURE [Sketcher::SketchObject] Sketch016
  ArcFitTolerance = 1e-06
  AttachmentSupport = -> [ShapeBinder]
  ExternalGeometry = -> [ShapeBinder]
  ExternalTypes = [0,0,0]
  FullyConstrained = true
  MakeInternals = false
  MapMode = 5
  Placement = pos=(3.5e-15,-1.2e-15,-18.5) rot=(1,0,0;3.14159rad)
  sketch-geometry (2):
    g0: Circle CenterX=-12 CenterY=7 CenterZ=0 NormalX=0 NormalY=0 NormalZ=1 AngleXU=0 Radius=1.6
    g1: Circle CenterX=-12 CenterY=-7 CenterZ=0 NormalX=0 NormalY=0 NormalZ=1 AngleXU=0 Radius=1.6
  constraints (4):
    c: Coincident(g0,g-21)
    c: Coincident(g1,g-22)
    c: Equal(g1,g0)
    c: Diameter(g0) = 3.2
FEATURE [PartDesign::Pad] Pad005
  Direction = (0,0,-1)
  Length = 3
  Length2 = 10
  Placement = pos=(3.5e-15,-1.2e-15,-10.5) rot=(0,0,1;0rad)
  Profile = -> Sketch016
  ReferenceAxis = -> Sketch016 [N_Axis]
  Refine = true
  SideType = 0
  Suppressed = false
  Type = 0
  Type2 = 0
FEATURE [Sketcher::SketchObject] Sketch017
  ArcFitTolerance = 1e-06
  AttachmentSupport = -> [Pad005]
  ExternalGeometry = -> [Pad005]
  ExternalTypes = [0,0,0]
  FullyConstrained = true
  MakeInternals = false
  MapMode = 5
  Placement = pos=(3.5e-15,-1.2e-15,-21.5) rot=(1,0,0;3.14159rad)
  sketch-geometry (16):
    g0: LineSegment StartX=-26 StartY=-5 StartZ=0 EndX=-26 EndY=-85 EndZ=0
    g1: LineSegment StartX=-6 StartY=-10.3923 StartZ=0 EndX=-6 EndY=-76.0557 EndZ=0
    g2: ArcOfCircle CenterX=-12 CenterY=-9e-16 CenterZ=0 NormalX=0 NormalY=0 NormalZ=1 AngleXU=0 Radius=12 StartAngle=3.57137 EndAngle=5.23599
    g3: LineSegment StartX=-22.9087 StartY=-5 StartZ=0 EndX=-26 EndY=-5 EndZ=0
    g4: ArcOfCircle CenterX=-14 CenterY=-85 CenterZ=0 NormalX=0 NormalY=0 NormalZ=1 AngleXU=0 Radius=12 StartAngle=3.14159 EndAngle=7.12425
    g5: Circle CenterX=-14 CenterY=-85 CenterZ=0 NormalX=0 NormalY=0 NormalZ=1 AngleXU=0 Radius=1.6
    g6: Circle [constr] CenterX=-14 CenterY=-85 CenterZ=0 NormalX=0 NormalY=0 NormalZ=1 AngleXU=0 Radius=7
    g7: LineSegment [constr] StartX=-9.05025 StartY=-80.0503 StartZ=0 EndX=-18.9497 EndY=-80.0503 EndZ=0
    g8: LineSegment [constr] StartX=-18.9497 StartY=-80.0503 StartZ=0 EndX=-18.9497 EndY=-89.9497 EndZ=0
    g9: LineSegment [constr] StartX=-18.9497 StartY=-89.9497 StartZ=0 EndX=-9.05025 EndY=-89.9497 EndZ=0
    g10: LineSegment [constr] StartX=-9.05025 StartY=-89.9497 StartZ=0 EndX=-9.05025 EndY=-80.0503 EndZ=0
    g11: Circle [constr] CenterX=-14 CenterY=-85 CenterZ=0 NormalX=0 NormalY=0 NormalZ=1 AngleXU=0 Radius=7
    g12: Circle CenterX=-18.9497 CenterY=-80.0503 CenterZ=0 NormalX=0 NormalY=0 NormalZ=1 AngleXU=0 Radius=1.6
    g13: Circle CenterX=-9.05025 CenterY=-80.0503 CenterZ=0 NormalX=0 NormalY=0 NormalZ=1 AngleXU=0 Radius=1.6
    g14: Circle CenterX=-9.05025 CenterY=-89.9497 CenterZ=0 NormalX=0 NormalY=0 NormalZ=1 AngleXU=0 Radius=1.6
    g15: Circle CenterX=-18.9497 CenterY=-89.9497 CenterZ=0 NormalX=0 NormalY=0 NormalZ=1 AngleXU=0 Radius=1.6
  constraints (40):
    c: Coincident(g0,g-3)
    c: Vertical(g0)
    c: PointOnObject(g1,g-4)
    c: Vertical(g1)
    c: Coincident(g2,g-4)
    c: Coincident(g2,g1)
    c: Coincident(g3,g2)
    c: Coincident(g3,g0)
    c: Horizontal(g3)
    c: Coincident(g4,g1)
    c: Tangent(g4,g0) = -1.5708
    c: Radius(g4) = 12
    c: Distance(g0,g1) = 20
    c: DistanceY(g4,g2) = 85
    c: Coincident(g5,g4)
    c: Coincident(g6,g4)
    c: Diameter(g5) = 3.2
    c: Coincident(g7,g8)
    c: Coincident(g8,g9)
    c: Coincident(g9,g10)
    c: Coincident(g10,g7)
    c: Equal(g7,g8)
    c: Equal(g7,g9)
    c: Equal(g7,g10)
    c: PointOnObject(g7,g11)
    c: PointOnObject(g8,g11)
    c: PointOnObject(g9,g11)
    c: PointOnObject(g10,g11)
    c: Coincident(g11,g4)
    c: PointOnObject(g10,g6)
    c: Horizontal(g7)
    c: Coincident(g12,g7)
    c: Coincident(g13,g7)
    c: Coincident(g14,g9)
    c: Coincident(g15,g8)
    c: Equal(g15,g14)
    c: Equal(g14,g13)
    c: Equal(g13,g12)
    c: Equal(g12,g5)
    c: Diameter(g6) = 14
FEATURE [PartDesign::Pad] Pad006
  BaseFeature = -> Pad005
  Direction = (0,0,-1)
  Length = 3
  Length2 = 10
  Placement = pos=(3.5e-15,-1.2e-15,-10.5) rot=(0,0,1;0rad)
  Profile = -> Sketch017
  ReferenceAxis = -> Sketch017 [N_Axis]
  Refine = true
  Reversed = true
  SideType = 0
  Suppressed = false
  Type = 0
  Type2 = 0
FEATURE [PartDesign::Fillet] Fillet003
  Base = -> Pad006 [Edge26,Edge38]
  BaseFeature = -> Pad006
  Placement = pos=(3.5e-15,-1.2e-15,-10.5) rot=(0,0,1;0rad)
  Radius = 6
  Refine = true
  SupportTransform = false
  Suppressed = false
  UseAllEdges = false
FEATURE [Sketcher::SketchObject] Sketch257
  ArcFitTolerance = 1e-06
  AttachmentSupport = -> [Fillet003]
  ExternalGeometry = -> [Fillet003]
  ExternalTypes = [0,0,0]
  FullyConstrained = true
  MakeInternals = false
  MapMode = 5
  Placement = pos=(3.5e-15,-1.2e-15,-21.5) rot=(1,0,0;3.14159rad)
  sketch-geometry (5):
    g0: ArcOfCircle CenterX=-12 CenterY=1e-16 CenterZ=0 NormalX=0 NormalY=0 NormalZ=1 AngleXU=0 Radius=12 StartAngle=5.54333 EndAngle=7.1064
    g1: LineSegment StartX=-3.84157 StartY=-8.8 StartZ=0 EndX=18 EndY=-8.8 EndZ=0
    g2: LineSegment StartX=18 StartY=-8.8 StartZ=0 EndX=18 EndY=8.8 EndZ=0
    g3: LineSegment StartX=18 StartY=8.8 StartZ=0 EndX=-3.84157 EndY=8.8 EndZ=0
    g4: LineSegment StartX=-3.84157 StartY=-8.8 StartZ=0 EndX=-3.1372 EndY=-8.09017 EndZ=0
  constraints (13):
    c: Coincident(g0,g-3)
    c: Coincident(g0,g-3)
    c: Coincident(g1,g-4)
    c: Horizontal(g1)
    c: Coincident(g2,g1)
    c: Vertical(g2)
    c: Coincident(g3,g2)
    c: Coincident(g3,g0)
    c: Horizontal(g3)
    c: PointOnObject(g-5,g2)
    c: Coincident(g4,g1)
    c: Coincident(g4,g0)
    c: Distance(g4,g4) = 1
FEATURE [PartDesign::Pocket] Pocket039
  BaseFeature = -> Fillet003
  Direction = (0,0,1)
  Length = 5
  Length2 = 5
  Placement = pos=(3.5e-15,-1.2e-15,-10.5) rot=(0,0,1;0rad)
  Profile = -> Sketch257
  ReferenceAxis = -> Sketch257 [N_Axis]
  Refine = true
  SideType = 0
  Suppressed = false
  Type = 0
  Type2 = 0
FEATURE [Sketcher::SketchObject] Sketch264
  ArcFitTolerance = 1e-06
  AttachmentSupport = -> [Pocket039]
  ExternalGeometry = -> [Pocket039]
  ExternalTypes = [0,0]
  FullyConstrained = true
  MakeInternals = false
  MapMode = 5
  Placement = pos=(3.5e-15,-1.2e-15,-21.5) rot=(1,0,0;3.14159rad)
  sketch-geometry (1):
    g0: Circle CenterX=-22 CenterY=-29 CenterZ=0 NormalX=0 NormalY=0 NormalZ=1 AngleXU=0 Radius=1.5
  constraints (3):
    c: Diameter(g0) = 3
    c: Distance(g0,g-3) = 4
    c: DistanceY(g-4,g0) = 56
FEATURE [PartDesign::Pocket] Pocket043
  BaseFeature = -> Pocket039
  Direction = (0,0,1)
  Length = 5
  Length2 = 5
  Placement = pos=(3.5e-15,-1.2e-15,-10.5) rot=(0,0,1;0rad)
  Profile = -> Sketch264
  ReferenceAxis = -> Sketch264 [N_Axis]
  Refine = true
  SideType = 0
  Suppressed = false
  Type = 0
  Type2 = 0
FEATURE [PartDesign::Body] Body006  label="arm-plate"
  AllowCompound = true
  Group = -> [ShapeBinder,Sketch016,Pad005,Sketch017,Pad006,Fillet003,Sketch257,Pocket039,Sketch264,Pocket043]
  Origin = -> Origin144
  Tip = -> Pocket043
COMPONENT P19 — same part as P18; its construction recipe is shown at P18.
COMPONENT P20 — recipe-attached ("servo-support001", modeled in this document).
Construction recipe (the document's own serialized feature program — sketch geometry with constraints, then the solid features built on it; lengths are millimeters unless a unit is written):

FEATURE [PartDesign::SubShapeBinder] Binder
  BindCopyOnChange = 0
  BindMode = 2
  ClaimChildren = false
  Context = -> Assembly [Body044.Binder.]
  Fuse = false
  MakeFace = true
  OffsetFill = false
  OffsetIntersection = false
  OffsetJoinType = 0
  OffsetOpenResult = false
  PartialLoad = false
  Refine = true
  Relative = false
  _Version = 2
FEATURE [Sketcher::SketchObject] Sketch247
  ArcFitTolerance = 1e-06
  AttachmentSupport = -> [Origin153]
  ExternalGeometry = -> [Binder]
  ExternalTypes = [0,0,0,0]
  FullyConstrained = true
  MakeInternals = false
  MapMode = 5
  Placement = pos=(0,0,0) rot=(1,0,0;1.5708rad)
  sketch-geometry (7):
    g0: Circle CenterX=20 CenterY=0 CenterZ=0 NormalX=0 NormalY=0 NormalZ=1 AngleXU=0 Radius=1.7
    g1: Circle CenterX=-16.383 CenterY=11.4715 CenterZ=0 NormalX=0 NormalY=0 NormalZ=1 AngleXU=0 Radius=1.7
    g2: Circle CenterX=-16.383 CenterY=-11.4715 CenterZ=0 NormalX=0 NormalY=0 NormalZ=1 AngleXU=0 Radius=1.7
    g3: LineSegment StartX=24 StartY=-20.75 StartZ=0 EndX=24 EndY=20.75 EndZ=0
    g4: LineSegment StartX=24 StartY=20.75 StartZ=0 EndX=-56 EndY=20.75 EndZ=0
    g5: LineSegment StartX=-56 StartY=20.75 StartZ=0 EndX=-56 EndY=-20.7501 EndZ=0
    g6: LineSegment StartX=-56 StartY=-20.7501 StartZ=0 EndX=24 EndY=-20.75 EndZ=0
  constraints (17):
    c: Coincident(g0,g-3)
    c: Coincident(g1,g-4)
    c: Coincident(g2,g-5)
    c: Equal(g2,g1)
    c: Equal(g1,g0)
    c: Diameter(g0) = 3.4
    c: Coincident(g3,g4)
    c: Horizontal(g4)
    c: Coincident(g4,g5)
    c: Vertical(g5)
    c: Coincident(g5,g6)
    c: Coincident(g6,g3)
    c: Symmetric(g3,g3,g-1)
    c: Equal(g6,g4)
    c: PointOnObject(g-6,g3)
    c: DistanceY(g3,g3) = 41.5
    c: Distance(g3,g5) = 80
FEATURE [PartDesign::Pad] Pad105
  Direction = (0,-1,2e-16)
  Length = 15
  Length2 = 10
  Profile = -> Sketch247
  ReferenceAxis = -> Sketch247 [N_Axis]
  Refine = true
  SideType = 0
  Suppressed = false
  Type = 0
  Type2 = 0
FEATURE [Sketcher::SketchObject] Sketch248
  ArcFitTolerance = 1e-06
  AttachmentSupport = -> [Pad105]
  ExternalGeometry = -> [Pad105]
  ExternalTypes = [0,0]
  FullyConstrained = true
  MakeInternals = false
  MapMode = 5
  Placement = pos=(0,-15,0) rot=(1,0,0;1.5708rad)
  sketch-geometry (8):
    g0: LineSegment StartX=-56 StartY=-20.7501 StartZ=0 EndX=-47 EndY=-20.7501 EndZ=0
    g1: LineSegment StartX=-47 StartY=-20.7501 StartZ=0 EndX=-47 EndY=-10.7501 EndZ=0
    g2: LineSegment StartX=-47 StartY=-10.7501 StartZ=0 EndX=-56 EndY=-10.7501 EndZ=0
    g3: LineSegment StartX=-56 StartY=-10.7501 StartZ=0 EndX=-56 EndY=-20.7501 EndZ=0
    g4: LineSegment StartX=-7 StartY=-20.75 StartZ=0 EndX=2 EndY=-20.75 EndZ=0
    g5: LineSegment StartX=2 StartY=-20.75 StartZ=0 EndX=2 EndY=-10.75 EndZ=0
    g6: LineSegment StartX=2 StartY=-10.75 StartZ=0 EndX=-7 EndY=-10.75 EndZ=0
    g7: LineSegment StartX=-7 StartY=-10.75 StartZ=0 EndX=-7 EndY=-20.75 EndZ=0
  constraints (23):
    c: Coincident(g0,g1)
    c: Coincident(g1,g2)
    c: Coincident(g2,g3)
    c: Coincident(g3,g0)
    c: Horizontal(g0)
    c: Horizontal(g2)
    c: Vertical(g1)
    c: Vertical(g3)
    c: Coincident(g0,g-3)
    c: Coincident(g4,g5)
    c: Coincident(g5,g6)
    c: Coincident(g6,g7)
    c: Coincident(g7,g4)
    c: Horizontal(g4)
    c: Horizontal(g6)
    c: Vertical(g5)
    c: Vertical(g7)
    c: PointOnObject(g4,g-4)
    c: Distance(g7,g1) = 40
    c: Distance(g5,g3) = 58
    c: Equal(g2,g6)
    c: DistanceY(g3,g3) = 10
    c: Equal(g7,g1)
FEATURE [PartDesign::Pad] Pad106
  BaseFeature = -> Pad105
  Direction = (0,-1,2e-16)
  Length = 20
  Length2 = 10
  Profile = -> Sketch248
  ReferenceAxis = -> Sketch248 [N_Axis]
  Refine = true
  SideType = 0
  Suppressed = false
  Type = 0
  Type2 = 0
FEATURE [PartDesign::Draft] Draft
  Angle = 30
  Base = -> Pad106 [Face15]
  BaseFeature = -> Pad106
  NeutralPlane = -> Pad106 [Face17]
  Refine = true
  Reversed = true
  SupportTransform = false
  Suppressed = false
FEATURE [Sketcher::SketchObject] Sketch249
  ArcFitTolerance = 1e-06
  AttachmentSupport = -> [Draft]
  ExternalGeometry = -> [Draft]
  ExternalTypes = [0,0,0]
  FullyConstrained = true
  MakeInternals = false
  MapMode = 5
  Placement = pos=(0,-4.6e-15,-20.7501) rot=(1,0,0;3.14159rad)
  sketch-geometry (11):
    g0: LineSegment [constr] StartX=-51.5 StartY=30 StartZ=0 EndX=-51.5 EndY=20 EndZ=0
    g1: LineSegment [constr] StartX=-51.5 StartY=20 StartZ=0 EndX=-2.5 EndY=20 EndZ=0
    g2: LineSegment [constr] StartX=-2.5 StartY=20 StartZ=0 EndX=-2.5 EndY=30 EndZ=0
    g3: LineSegment [constr] StartX=-2.5 StartY=30 StartZ=0 EndX=-51.5 EndY=30 EndZ=0
    g4: GeomPoint [constr] X=-27 Y=25 Z=0
    g5: LineSegment [constr] StartX=-27 StartY=30 StartZ=0 EndX=-27 EndY=20 EndZ=0
    g6: LineSegment [constr] StartX=-51.5 StartY=25 StartZ=0 EndX=-2.5 EndY=25 EndZ=0
    g7: Circle CenterX=-51.5 CenterY=30 CenterZ=0 NormalX=0 NormalY=0 NormalZ=1 AngleXU=0 Radius=2.25
    g8: Circle CenterX=-51.5 CenterY=20 CenterZ=0 NormalX=0 NormalY=0 NormalZ=1 AngleXU=0 Radius=2.25
    g9: Circle CenterX=-2.5 CenterY=30 CenterZ=0 NormalX=0 NormalY=0 NormalZ=1 AngleXU=0 Radius=2.25
    g10: Circle CenterX=-2.5 CenterY=20 CenterZ=0 NormalX=0 NormalY=0 NormalZ=1 AngleXU=0 Radius=2.25
  constraints (23):
    c: Coincident(g0,g1)
    c: Coincident(g1,g2)
    c: Coincident(g2,g3)
    c: Coincident(g3,g0)
    c: Vertical(g0)
    c: Horizontal(g1)
    c: DistanceY(g2,g2) = 10
    c: DistanceX(g3,g3) = 49
    c: Symmetric(g0,g2,g4)
    c: Symmetric(g3,g3,g5)
    c: Symmetric(g1,g1,g5)
    c: Symmetric(g-3,g-5,g5)
    c: Symmetric(g0,g0,g6)
    c: Symmetric(g2,g2,g6)
    c: Symmetric(g-3,g-4,g6)
    c: Coincident(g7,g0)
    c: Coincident(g8,g0)
    c: Coincident(g9,g2)
    c: Coincident(g10,g1)
    c: Equal(g10,g9)
    c: Equal(g9,g7)
    c: Equal(g7,g8)
    c: Diameter(g7) = 4.5
FEATURE [PartDesign::Pocket] Pocket034
  BaseFeature = -> Draft
  Direction = (0,0,1)
  Length = 5
  Length2 = 5
  Profile = -> Sketch249
  ReferenceAxis = -> Sketch249 [N_Axis]
  Refine = true
  SideType = 0
  Suppressed = false
  Type = 1
  Type2 = 0
FEATURE [PartDesign::Chamfer] Chamfer030
  Angle = 45
  Base = -> Pocket034 [Edge32,Edge45,Edge44,Edge33,Edge38,Edge37,Edge52,Edge51]
  BaseFeature = -> Pocket034
  ChamferType = 0
  FlipDirection = false
  Refine = true
  Size = 0.4
  Size2 = 1
  SupportTransform = false
  Suppressed = false
  UseAllEdges = false
FEATURE [PartDesign::Mirrored] Mirrored
  BaseFeature = -> Chamfer030
  MirrorPlane = -> Sketch248 [H_Axis]
  Originals = -> [Pad106,Draft,Pocket034,Chamfer030]
  Refine = true
  Suppressed = false
  TransformMode = 0
FEATURE [PartDesign::Chamfer] Chamfer031
  Angle = 45
  Base = -> Mirrored [Edge23,Edge1]
  BaseFeature = -> Mirrored
  ChamferType = 0
  FlipDirection = false
  Refine = true
  Size = 6
  Size2 = 1
  SupportTransform = false
  Suppressed = false
  UseAllEdges = false
FEATURE [Sketcher::SketchObject] Sketch250
  ArcFitTolerance = 1e-06
  AttachmentSupport = -> [Chamfer031]
  ExternalGeometry = -> [Chamfer031]
  ExternalTypes = [0]
  FullyConstrained = true
  MakeInternals = false
  MapMode = 5
  Placement = pos=(-56,0,0) rot=(0.57735,-0.57735,-0.57735;2.0944rad)
  sketch-geometry (5):
    g0: LineSegment StartX=24 StartY=-7 StartZ=0 EndX=24 EndY=7 EndZ=0
    g1: LineSegment StartX=24 StartY=7 StartZ=0 EndX=6 EndY=7 EndZ=0
    g2: LineSegment StartX=6 StartY=7 StartZ=0 EndX=6 EndY=-7 EndZ=0
    g3: LineSegment StartX=6 StartY=-7 StartZ=0 EndX=24 EndY=-7 EndZ=0
    g4: GeomPoint [constr] X=15 Y=8e-16 Z=0
  constraints (12):
    c: Coincident(g0,g1)
    c: Coincident(g1,g2)
    c: Coincident(g2,g3)
    c: Coincident(g3,g0)
    c: Vertical(g0)
    c: Vertical(g2)
    c: Horizontal(g1)
    c: Horizontal(g3)
    c: Symmetric(g2,g0,g4)
    c: Symmetric(g-3,g-3,g4)
    c: Distance(g2,g2) = 14
    c: Distance(g1,g-2) = 6
FEATURE [PartDesign::Pocket] Pocket035
  BaseFeature = -> Chamfer031
  Direction = (1,0,0)
  Length = 60
  Length2 = 5
  Profile = -> Sketch250
  ReferenceAxis = -> Sketch250 [N_Axis]
  Refine = true
  SideType = 0
  Suppressed = false
  Type = 0
  Type2 = 0
FEATURE [PartDesign::Chamfer] Chamfer032
  Angle = 45
  Base = -> Pocket035 [Edge48,Edge47,Edge49]
  BaseFeature = -> Pocket035
  ChamferType = 0
  FlipDirection = false
  Refine = true
  Size = 2
  Size2 = 1
  SupportTransform = false
  Suppressed = false
  UseAllEdges = false
FEATURE [PartDesign::Fillet] Fillet025
  Base = -> Chamfer032 [Edge65]
  BaseFeature = -> Chamfer032
  Radius = 4
  Refine = true
  SupportTransform = false
  Suppressed = false
  UseAllEdges = false
FEATURE [PartDesign::Chamfer] Chamfer033
  Angle = 45
  Base = -> Fillet025 [Edge1,Edge8]
  BaseFeature = -> Fillet025
  ChamferType = 0
  FlipDirection = false
  Refine = true
  Size = 1
  Size2 = 1
  SupportTransform = false
  Suppressed = false
  UseAllEdges = false
FEATURE [PartDesign::Chamfer] Chamfer034
  Angle = 45
  Base = -> Chamfer033 [Edge18,Edge11]
  BaseFeature = -> Chamfer033
  ChamferType = 0
  FlipDirection = false
  Refine = true
  Size = 2
  Size2 = 1
  SupportTransform = false
  Suppressed = false
  UseAllEdges = false
FEATURE [PartDesign::Chamfer] Chamfer035
  Angle = 45
  Base = -> Chamfer034 [Edge65,Edge57]
  BaseFeature = -> Chamfer034
  ChamferType = 0
  FlipDirection = false
  Refine = true
  Size = 2
  Size2 = 1
  SupportTransform = false
  Suppressed = false
  UseAllEdges = false
FEATURE [Sketcher::SketchObject] Sketch251
  ArcFitTolerance = 1e-06
  AttachmentSupport = -> [Chamfer035]
  ExternalGeometry = -> [Chamfer035]
  ExternalTypes = [0,0]
  FullyConstrained = true
  MakeInternals = false
  MapMode = 5
  Placement = pos=(-56,0,0) rot=(0.57735,-0.57735,-0.57735;2.0944rad)
  sketch-geometry (10):
    g0: LineSegment [constr] StartX=7 StartY=20.75 StartZ=0 EndX=15 EndY=30.75 EndZ=0
    g1: LineSegment [constr] StartX=15 StartY=20.75 StartZ=0 EndX=15 EndY=30.75 EndZ=0
    g2: LineSegment StartX=15 StartY=20.75 StartZ=0 EndX=7 EndY=20.75 EndZ=0
    g3: LineSegment StartX=7 StartY=20.75 StartZ=0 EndX=14 EndY=29.5 EndZ=0
    g4: LineSegment StartX=14 StartY=29.5 StartZ=0 EndX=15 EndY=29.5 EndZ=0
    g5: LineSegment StartX=15 StartY=29.5 StartZ=0 EndX=15 EndY=20.75 EndZ=0
    g6: LineSegment StartX=15 StartY=-20.7501 StartZ=0 EndX=15 EndY=-29.5001 EndZ=0
    g7: LineSegment StartX=15 StartY=-29.5001 StartZ=0 EndX=14 EndY=-29.5001 EndZ=0
    g8: LineSegment StartX=7 StartY=-20.7501 StartZ=0 EndX=14 EndY=-29.5001 EndZ=0
    g9: LineSegment StartX=7 StartY=-20.7501 StartZ=0 EndX=15 EndY=-20.7501 EndZ=0
  constraints (27):
    c: PointOnObject(g0,g-3)
    c: Coincident(g1,g-3)
    c: Coincident(g1,g0)
    c: Coincident(g2,g1)
    c: Coincident(g2,g0)
    c: Vertical(g1)
    c: DistanceY(g1,g1) = 10
    c: DistanceX(g2,g2) = 8
    c: Coincident(g3,g0)
    c: PointOnObject(g3,g0)
    c: Coincident(g4,g3)
    c: PointOnObject(g4,g1)
    c: Coincident(g5,g4)
    c: Coincident(g5,g1)
    c: Perpendicular(g5,g4)
    c: Distance(g4,g4) = 1
    c: Coincident(g6,g-4)
    c: Coincident(g7,g6)
    c: PointOnObject(g8,g-4)
    c: Coincident(g8,g7)
    c: Coincident(g9,g8)
    c: Coincident(g9,g6)
    c: Vertical(g6)
    c: Perpendicular(g6,g7)
    c: Equal(g6,g5)
    c: Equal(g3,g8)
    c: Equal(g7,g4)
FEATURE [PartDesign::Pad] Pad107
  BaseFeature = -> Chamfer035
  Direction = (-1,0,0)
  Length = 52
  Length2 = 10
  Profile = -> Sketch251
  ReferenceAxis = -> Sketch251 [N_Axis]
  Refine = true
  Reversed = true
  SideType = 0
  Suppressed = false
  Type = 0
  Type2 = 0
FEATURE [PartDesign::Draft] Draft001
  Angle = 50
  Base = -> Pad107 [Face76]
  BaseFeature = -> Pad107
  NeutralPlane = -> Pad107 [Face77]
  Refine = true
  Reversed = true
  SupportTransform = false
  Suppressed = false
FEATURE [PartDesign::Draft] Draft002
  Angle = 50
  Base = -> Draft001 [Face82]
  BaseFeature = -> Draft001
  NeutralPlane = -> Draft001 [Face83]
  Refine = true
  Reversed = true
  SupportTransform = false
  Suppressed = false
FEATURE [PartDesign::Fillet] Fillet026
  Base = -> Draft002 [Edge202,Edge192]
  BaseFeature = -> Draft002
  Radius = 5
  Refine = true
  SupportTransform = false
  Suppressed = false
  UseAllEdges = false
FEATURE [Sketcher::SketchObject] Sketch252
  ArcFitTolerance = 1e-06
  AttachmentSupport = -> [Fillet026]
  ExternalGeometry = -> [Fillet026]
  ExternalTypes = [0,0]
  FullyConstrained = true
  MakeInternals = false
  MapMode = 5
  Placement = pos=(-56,0,0) rot=(0.57735,-0.57735,-0.57735;2.0944rad)
  sketch-geometry (10):
    g0: LineSegment StartX=23.5 StartY=23.7501 StartZ=0 EndX=23.5 EndY=17.7501 EndZ=0
    g1: LineSegment StartX=23.5 StartY=17.7501 StartZ=0 EndX=26.5 EndY=17.7501 EndZ=0
    g2: LineSegment StartX=26.5 StartY=17.7501 StartZ=0 EndX=26.5 EndY=23.7501 EndZ=0
    g3: LineSegment StartX=26.5 StartY=23.7501 StartZ=0 EndX=23.5 EndY=23.7501 EndZ=0
    g4: GeomPoint [constr] X=25 Y=20.7501 Z=0
    g5: LineSegment StartX=23.5 StartY=-17.7501 StartZ=0 EndX=23.5 EndY=-23.7501 EndZ=0
    g6: LineSegment StartX=23.5 StartY=-23.7501 StartZ=0 EndX=26.5 EndY=-23.7501 EndZ=0
    g7: LineSegment StartX=26.5 StartY=-23.7501 StartZ=0 EndX=26.5 EndY=-17.7501 EndZ=0
    g8: LineSegment StartX=26.5 StartY=-17.7501 StartZ=0 EndX=23.5 EndY=-17.7501 EndZ=0
    g9: GeomPoint [constr] X=25 Y=-20.7501 Z=0
  constraints (24):
    c: Coincident(g0,g1)
    c: Coincident(g1,g2)
    c: Coincident(g2,g3)
    c: Coincident(g3,g0)
    c: Vertical(g0)
    c: Vertical(g2)
    c: Horizontal(g1)
    c: Horizontal(g3)
    c: Symmetric(g2,g0,g4)
    c: Symmetric(g-4,g-3,g4)
    c: Distance(g3,g3) = 3
    c: Distance(g1,g-4) = 3
    c: Coincident(g5,g6)
    c: Coincident(g6,g7)
    c: Coincident(g7,g8)
    c: Coincident(g8,g5)
    c: Vertical(g5)
    c: Vertical(g7)
    c: Horizontal(g6)
    c: Horizontal(g8)
    c: Symmetric(g7,g5,g9)
    c: Equal(g2,g7)
    c: Equal(g8,g1)
    c: Symmetric(g9,g4,g-1)
FEATURE [PartDesign::Pocket] Pocket036
  BaseFeature = -> Fillet026
  Direction = (1,0,0)
  Length = 5
  Length2 = 5
  Profile = -> Sketch252
  ReferenceAxis = -> Sketch252 [N_Axis]
  Refine = true
  SideType = 0
  Suppressed = false
  Type = 1
  Type2 = 0
FEATURE [Sketcher::SketchObject] Sketch253
  ArcFitTolerance = 1e-06
  AttachmentSupport = -> [Pocket036]
  ExternalGeometry = -> [Binder]
  ExternalTypes = [0,0]
  FullyConstrained = true
  MakeInternals = false
  MapMode = 5
  Placement = pos=(0,0,0) rot=(0,0.707107,0.707107;3.14159rad)
  sketch-geometry (2):
    g0: Circle CenterX=-15 CenterY=-11.547 CenterZ=0 NormalX=0 NormalY=0 NormalZ=1 AngleXU=0 Radius=3.5
    g1: Circle [constr] CenterX=-15 CenterY=11.547 CenterZ=0 NormalX=0 NormalY=0 NormalZ=1 AngleXU=0 Radius=3.55023
  constraints (5):
    c: PointOnObject(g-3,g1)
    c: PointOnObject(g-4,g1)
    c: PointOnObject(g-4,g1)
    c: Symmetric(g0,g1,g-1)
    c: Diameter(g0) = 7
FEATURE [PartDesign::Pocket] Pocket037
  BaseFeature = -> Pocket036
  Direction = (0,-1,0)
  Length = 4
  Length2 = 5
  Profile = -> Sketch253
  ReferenceAxis = -> Sketch253 [N_Axis]
  Refine = true
  SideType = 0
  Suppressed = false
  Type = 0
  Type2 = 0
FEATURE [Sketcher::SketchObject] Sketch254
  ArcFitTolerance = 1e-06
  AttachmentSupport = -> [Origin153]
  ExternalGeometry = -> [Pocket037]
  ExternalTypes = [0]
  FullyConstrained = true
  MakeInternals = false
  MapMode = 5
  sketch-geometry (4):
    g0: LineSegment StartX=24 StartY=-3 StartZ=0 EndX=46.2163 EndY=-8.95284 EndZ=0
    g1: LineSegment StartX=46.2163 StartY=-8.95284 StartZ=0 EndX=46.2163 EndY=0 EndZ=0
    g2: LineSegment StartX=24 StartY=-3 StartZ=0 EndX=24 EndY=-4e-16 EndZ=0
    g3: LineSegment StartX=46.2163 StartY=0 StartZ=0 EndX=24 EndY=-4e-16 EndZ=0
  constraints (11):
    c: PointOnObject(g0,g-3)
    c: Coincident(g1,g0)
    c: PointOnObject(g1,g-1)
    c: Vertical(g1)
    c: Distance(g0,g0) = 23
    c: Coincident(g2,g0)
    c: Coincident(g2,g-3)
    c: Coincident(g3,g1)
    c: Coincident(g3,g2)
    c: Distance(g2,g2) = 3
    c: Angle(g0,g3) = 0.261799
FEATURE [PartDesign::Pad] Pad108
  BaseFeature = -> Pocket037
  Direction = (0,0,1)
  Length = 13
  Length2 = 10
  Profile = -> Sketch254
  ReferenceAxis = -> Sketch254 [N_Axis]
  Refine = true
  SideType = 2
  Suppressed = false
  Type = 0
  Type2 = 0
FEATURE [Sketcher::SketchObject] Sketch255
  ArcFitTolerance = 1e-06
  AttachmentSupport = -> [Pad108]
  ExternalGeometry = -> [Pad108]
  ExternalTypes = [0,0]
  FullyConstrained = true
  MakeInternals = false
  MapMode = 5
  Placement = pos=(46.2163,0,0) rot=(0.57735,0.57735,0.57735;2.0944rad)
  sketch-geometry (8):
    g0: LineSegment StartX=0 StartY=6.5 StartZ=0 EndX=0 EndY=9.5 EndZ=0
    g1: LineSegment StartX=0 StartY=9.5 StartZ=0 EndX=-8.95284 EndY=9.5 EndZ=0
    g2: LineSegment StartX=-8.95284 StartY=9.5 StartZ=0 EndX=-8.95284 EndY=6.5 EndZ=0
    g3: LineSegment StartX=-8.95284 StartY=6.5 StartZ=0 EndX=0 EndY=6.5 EndZ=0
    g4: LineSegment StartX=-8.95284 StartY=-6.5 StartZ=0 EndX=-8.95284 EndY=-9.5 EndZ=0
    g5: LineSegment StartX=-8.95284 StartY=-9.5 StartZ=0 EndX=0 EndY=-9.5 EndZ=0
    g6: LineSegment StartX=0 StartY=-9.5 StartZ=0 EndX=0 EndY=-6.5 EndZ=0
    g7: LineSegment StartX=0 StartY=-6.5 StartZ=0 EndX=-8.95284 EndY=-6.5 EndZ=0
  constraints (21):
    c: Coincident(g0,g1)
    c: Coincident(g1,g2)
    c: Coincident(g2,g3)
    c: Coincident(g3,g0)
    c: Vertical(g0)
    c: Vertical(g2)
    c: Horizontal(g1)
    c: Coincident(g0,g-3)
    c: Coincident(g2,g-3)
    c: Coincident(g4,g5)
    c: Coincident(g5,g6)
    c: Coincident(g6,g7)
    c: Coincident(g7,g4)
    c: Vertical(g4)
    c: Vertical(g6)
    c: Horizontal(g5)
    c: Horizontal(g7)
    c: Coincident(g4,g-4)
    c: PointOnObject(g5,g-2)
    c: Equal(g2,g4)
    c: Distance(g0,g0) = 3
FEATURE [PartDesign::Pad] Pad109
  BaseFeature = -> Pad108
  Direction = (1,0,0)
  Length = 23
  Length2 = 10
  Profile = -> Sketch255
  ReferenceAxis = -> Sketch255 [N_Axis]
  Refine = true
  Reversed = true
  SideType = 0
  Suppressed = false
  Type = 0
  Type2 = 0
FEATURE [PartDesign::Draft] Draft003
  Angle = 10
  Base = -> Pad109 [Face64]
  BaseFeature = -> Pad109
  NeutralPlane = -> Pad109 [Face105]
  Refine = true
  SupportTransform = false
  Suppressed = false
FEATURE [PartDesign::Draft] Draft004
  Angle = 10
  Base = -> Draft003 [Face70]
  BaseFeature = -> Draft003
  NeutralPlane = -> Draft003 [Face105]
  Refine = true
  SupportTransform = false
  Suppressed = false
FEATURE [PartDesign::Fillet] Fillet027
  Base = -> Draft004 [Edge229,Edge218]
  BaseFeature = -> Draft004
  Radius = 2
  Refine = true
  SupportTransform = false
  Suppressed = false
  UseAllEdges = false
FEATURE [Sketcher::SketchObject] Sketch256
  ArcFitTolerance = 1e-06
  AttachmentSupport = -> [Fillet027]
  ExternalGeometry = -> [Fillet027]
  ExternalTypes = [0]
  FullyConstrained = true
  MakeInternals = false
  MapMode = 5
  Placement = pos=(0.857695,3.20096,0) rot=(0.983106,-0.129428,-0.129428;1.58783rad)
  sketch-geometry (1):
    g0: Circle CenterX=36.9587 CenterY=0 CenterZ=0 NormalX=0 NormalY=0 NormalZ=1 AngleXU=0 Radius=2.25
  constraints (3):
    c: PointOnObject(g0,g-1)
    c: Diameter(g0) = 4.5
    c: Distance(g0,g-3) = 13
FEATURE [PartDesign::Pocket] Pocket038
  BaseFeature = -> Fillet027
  Direction = (0.258819,0.965926,0)
  Length = 8
  Length2 = 5
  Profile = -> Sketch256
  ReferenceAxis = -> Sketch256 [N_Axis]
  Refine = true
  SideType = 0
  Suppressed = false
  Type = 0
  Type2 = 0
FEATURE [PartDesign::Fillet] Fillet028
  Base = -> Pocket038 [Edge38]
  BaseFeature = -> Pocket038
  Radius = 2
  Refine = true
  SupportTransform = false
  Suppressed = false
  UseAllEdges = false
FEATURE [PartDesign::Chamfer] Chamfer036
  Angle = 45
  Base = -> Fillet028 [Edge43,Edge37]
  BaseFeature = -> Fillet028
  ChamferType = 0
  FlipDirection = false
  Refine = true
  Size = 0.6
  Size2 = 1
  SupportTransform = false
  Suppressed = false
  UseAllEdges = false
FEATURE [PartDesign::Body] Body044  label="servo-support"
  AllowCompound = true
  Group = -> [Binder,Sketch247,Pad105,Sketch248,Pad106,Draft,Sketch249,Pocket034,Chamfer030,Mirrored,Chamfer031,Sketch250,Pocket035,Chamfer032,Fillet025,Chamfer033,Chamfer034,Chamfer035,Sketch251,Pad107,Draft001,Draft002,Fillet026,Sketch252,Pocket036,Sketch253,Pocket037,Sketch254,Pad108,Sketch255,Pad109,Draft003,Draft004,Fillet027,Sketch256,Pocket038,Fillet028,Chamfer036]
  Origin = -> Origin153
  Placement = pos=(-106,0,0) rot=(0,0,1;0rad)
  Tip = -> Chamfer036
PROVENANCE & LICENSES
A FreeCAD (.FCStd) document from a public repository crawl; recipes are the document's own serialized feature recipes (and, for linked parts, companion documents' recipes).
License: as declared in the source repository (recorded in the dataset sidecar).
